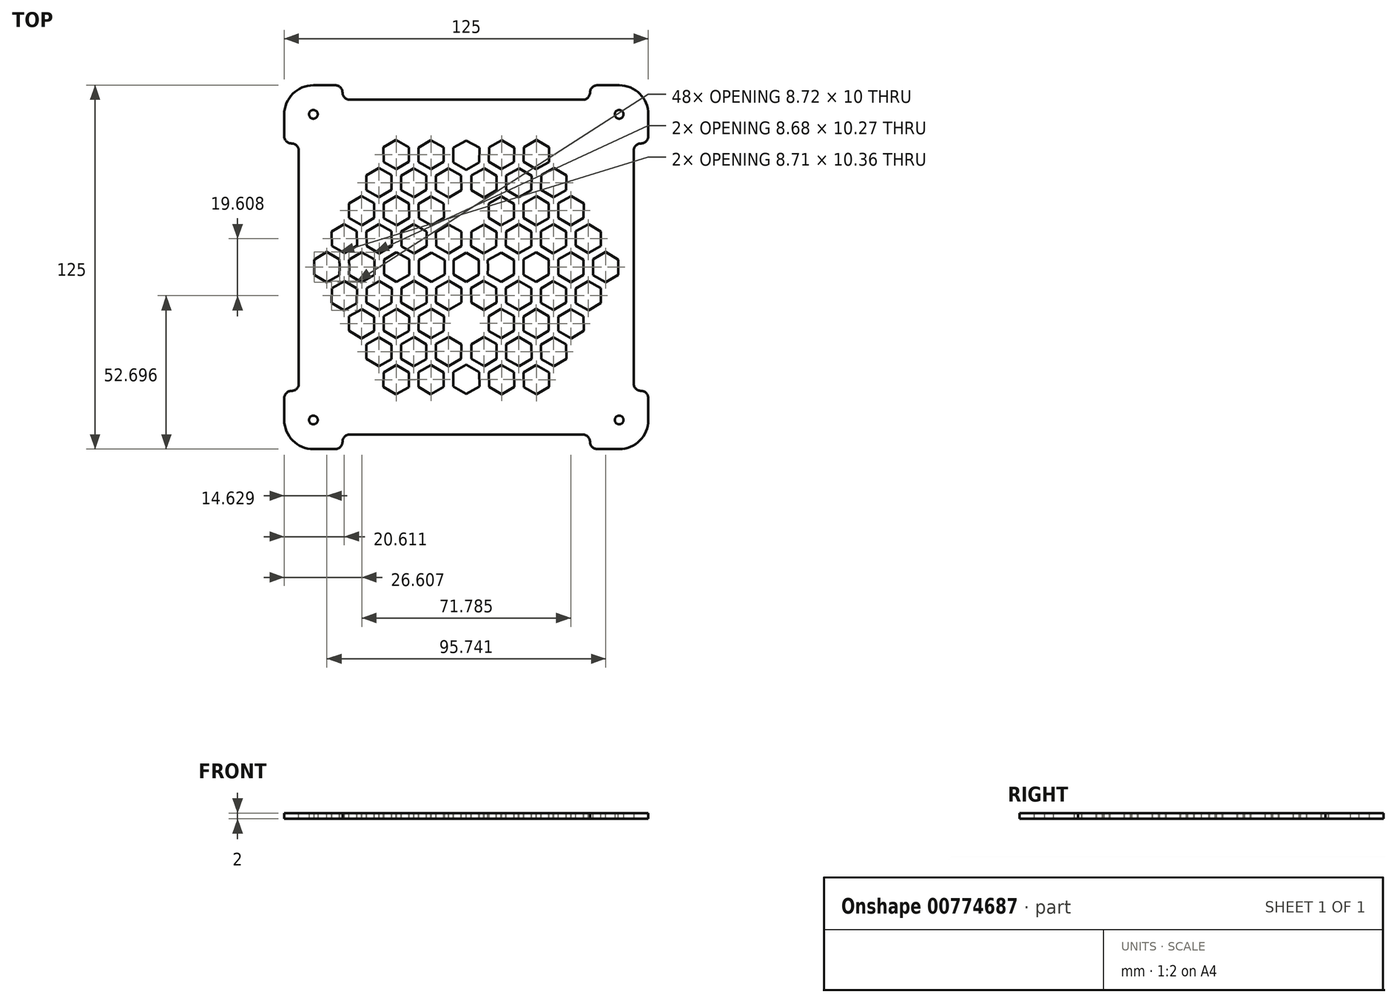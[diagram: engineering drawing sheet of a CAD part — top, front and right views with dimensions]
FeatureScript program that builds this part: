
annotation { "Feature Type Name" : "Feature", "Feature Type Description" : "" }
export const myFeature = defineFeature(function(context is Context, id is Id, definition is map)
    precondition{}
    {
        {
            var Q0;
            Q0=qCreatedBy(makeId("Top.planeOp"),FACE);
            var sketch = newSketch(context, id + "F0", { "sketchPlane" : qUnion([Q0])});
            skLineSegment(sketch, "E0.bottom", {"start": v(-52.5, 52.5) * mm, "end": v(52.5, 52.5) * mm});
            skLineSegment(sketch, "E0.top", {"start": v(-52.5, -52.5) * mm, "end": v(52.5, -52.5) * mm});
            skLineSegment(sketch, "E0.left", {"start": v(-52.5, 52.5) * mm, "end": v(-52.5, -52.5) * mm});
            skLineSegment(sketch, "E0.right", {"start": v(52.5, 52.5) * mm, "end": v(52.5, -52.5) * mm});
            skPoint(sketch, "E0.middle", {"position": v(0, 0) * mm});
            skCircle(sketch, "E1", {"center": v(0, 0) * mm, "radius": 52.5 * mm});
            skCircle(sketch, "E2", {"center": v(-52.5, 52.5) * mm, "radius": 1.5 * mm});
            skCircle(sketch, "E3", {"center": v(52.5, 52.5) * mm, "radius": 1.5 * mm});
            skCircle(sketch, "E4", {"center": v(52.5, -52.5) * mm, "radius": 1.5 * mm});
            skCircle(sketch, "E5", {"center": v(-52.5, -52.5) * mm, "radius": 1.5 * mm});
            skLineSegment(sketch, "E6.bottom", {"start": v(-62.5, 62.5) * mm, "end": v(-42.5, 62.5) * mm});
            skLineSegment(sketch, "E6.top", {"start": v(-62.5, 42.5) * mm, "end": v(-42.5, 42.5) * mm});
            skLineSegment(sketch, "E6.left", {"start": v(-62.5, 62.5) * mm, "end": v(-62.5, 42.5) * mm});
            skLineSegment(sketch, "E6.right", {"start": v(-42.5, 62.5) * mm, "end": v(-42.5, 42.5) * mm});
            skLineSegment(sketch, "E7.bottom", {"start": v(62.5, 62.5) * mm, "end": v(42.5, 62.5) * mm});
            skLineSegment(sketch, "E7.top", {"start": v(62.5, 42.5) * mm, "end": v(42.5, 42.5) * mm});
            skLineSegment(sketch, "E7.left", {"start": v(62.5, 62.5) * mm, "end": v(62.5, 42.5) * mm});
            skLineSegment(sketch, "E7.right", {"start": v(42.5, 62.5) * mm, "end": v(42.5, 42.5) * mm});
            skLineSegment(sketch, "E8.bottom", {"start": v(62.5, -42.5) * mm, "end": v(42.5, -42.5) * mm});
            skLineSegment(sketch, "E8.top", {"start": v(62.5, -62.5) * mm, "end": v(42.5, -62.5) * mm});
            skLineSegment(sketch, "E8.left", {"start": v(62.5, -42.5) * mm, "end": v(62.5, -62.5) * mm});
            skLineSegment(sketch, "E8.right", {"start": v(42.5, -42.5) * mm, "end": v(42.5, -62.5) * mm});
            skLineSegment(sketch, "E9.bottom", {"start": v(-62.5, -42.5) * mm, "end": v(-42.5, -42.5) * mm});
            skLineSegment(sketch, "E9.top", {"start": v(-62.5, -62.5) * mm, "end": v(-42.5, -62.5) * mm});
            skLineSegment(sketch, "E9.left", {"start": v(-62.5, -42.5) * mm, "end": v(-62.5, -62.5) * mm});
            skLineSegment(sketch, "E9.right", {"start": v(-42.5, -42.5) * mm, "end": v(-42.5, -62.5) * mm});
            skFitSpline(sketch, "E10", {"points": [v(0, 75.36) * mm, v(0, -75.45) * mm], "startDerivative": vector(0, -150.8) * mm, "endDerivative": vector(0, -150.8) * mm, "construction": true});
            skFitSpline(sketch, "E11", {"points": [v(-75.08, 0) * mm, v(75.41, 0) * mm], "startDerivative": vector(150.49, 0) * mm, "endDerivative": vector(150.49, 0) * mm, "construction": true});
            skLineSegment(sketch, "E12.bottom", {"start": v(-57.5, 57.5) * mm, "end": v(57.5, 57.5) * mm});
            skLineSegment(sketch, "E12.top", {"start": v(-57.5, -57.5) * mm, "end": v(57.5, -57.5) * mm});
            skLineSegment(sketch, "E12.left", {"start": v(-57.5, 57.5) * mm, "end": v(-57.5, -57.5) * mm});
            skLineSegment(sketch, "E12.right", {"start": v(57.5, 57.5) * mm, "end": v(57.5, -57.5) * mm});
            skSolve(sketch);
        }
        {
            var Q0;
            {var subQ0=sQuery(id+"F0.wireOp",EDGE,"E1");var subQ1=makeQuery(id+"F0.imprint","INTERSECT",VERTEX,{"derivedFrom":[sQuery(id+"F0.wireOp",EDGE,"E0.bottom"),subQ0]});Q0=makeQuery(id+"F0.imprint","IMPRINT",FACE,{"disambiguationData":[TD([[makeQuery(id+"F0.imprint","IMPRINT",EDGE,{"disambiguationData":[TD([[subQ1,1.0]])],"derivedFrom":subQ0}),1.0]])]});}
            var sketch = newSketch(context, id + "F1", { "sketchPlane" : qUnion([Q0])});
            skLineSegment(sketch, "E13.0", {"start": v(-4.36, 2.45) * mm, "end": v(0, 5) * mm});
            skLineSegment(sketch, "E13.5", {"start": v(-4.36, 0) * mm, "end": v(-4.36, 2.45) * mm});
            skPoint(sketch, "E13.0.midPoint", {"position": v(-2.18, 3.73) * mm});
            skLineSegment(sketch, "E14.1.0.0", {"start": v(-16.32, 2.5) * mm, "end": v(-12.02, 5.05) * mm});
            skLineSegment(sketch, "E14.1.0.2", {"start": v(-16.33, 0) * mm, "end": v(-16.32, 2.5) * mm});
            skLineSegment(sketch, "E14.1.0.4", {"start": v(-7.4, 2.45) * mm, "end": v(-7.42, 0) * mm});
            skLineSegment(sketch, "E14.1.0.5", {"start": v(-12.02, 5.05) * mm, "end": v(-7.4, 2.45) * mm});
            skLineSegment(sketch, "E14.1.1.0", {"start": v(-10.37, 12.12) * mm, "end": v(-6.07, 14.67) * mm});
            skLineSegment(sketch, "E14.1.1.1", {"start": v(-5.96, 4.67) * mm, "end": v(-10.32, 7.12) * mm});
            skLineSegment(sketch, "E14.1.1.2", {"start": v(-10.32, 7.12) * mm, "end": v(-10.37, 12.12) * mm});
            skLineSegment(sketch, "E14.1.1.3", {"start": v(-1.66, 7.22) * mm, "end": v(-5.96, 4.67) * mm});
            skLineSegment(sketch, "E14.1.1.4", {"start": v(-1.71, 12.22) * mm, "end": v(-1.66, 7.22) * mm});
            skLineSegment(sketch, "E14.1.1.5", {"start": v(-6.07, 14.67) * mm, "end": v(-1.71, 12.22) * mm});
            skLineSegment(sketch, "E14.1.2.0", {"start": v(-4.43, 21.74) * mm, "end": v(0, 24.24) * mm});
            skLineSegment(sketch, "E14.1.2.1", {"start": v(-0.02, 14.29) * mm, "end": v(-4.37, 16.74) * mm});
            skLineSegment(sketch, "E14.1.2.2", {"start": v(-4.37, 16.74) * mm, "end": v(-4.43, 21.74) * mm});
            skLineSegment(sketch, "E14.2.0.0", {"start": v(-28.27, 2.54) * mm, "end": v(-23.97, 5.1) * mm});
            skLineSegment(sketch, "E14.2.0.2", {"start": v(-28.28, 0) * mm, "end": v(-28.27, 2.54) * mm});
            skLineSegment(sketch, "E14.2.0.4", {"start": v(-19.61, 2.64) * mm, "end": v(-19.63, 0) * mm});
            skLineSegment(sketch, "E14.2.0.5", {"start": v(-23.97, 5.1) * mm, "end": v(-19.61, 2.64) * mm});
            skLineSegment(sketch, "E14.2.1.0", {"start": v(-22.33, 12.16) * mm, "end": v(-18.03, 14.71) * mm});
            skLineSegment(sketch, "E14.2.1.1", {"start": v(-17.92, 4.71) * mm, "end": v(-22.27, 7.16) * mm});
            skLineSegment(sketch, "E14.2.1.2", {"start": v(-22.27, 7.16) * mm, "end": v(-22.33, 12.16) * mm});
            skLineSegment(sketch, "E14.2.1.3", {"start": v(-13.61, 7.26) * mm, "end": v(-17.92, 4.71) * mm});
            skLineSegment(sketch, "E14.2.1.4", {"start": v(-13.67, 12.26) * mm, "end": v(-13.61, 7.26) * mm});
            skLineSegment(sketch, "E14.2.1.5", {"start": v(-18.03, 14.71) * mm, "end": v(-13.67, 12.26) * mm});
            skLineSegment(sketch, "E14.2.2.0", {"start": v(-16.39, 21.79) * mm, "end": v(-12.09, 24.33) * mm});
            skLineSegment(sketch, "E14.2.2.1", {"start": v(-11.97, 14.33) * mm, "end": v(-16.33, 16.79) * mm});
            skLineSegment(sketch, "E14.2.2.2", {"start": v(-16.33, 16.79) * mm, "end": v(-16.39, 21.79) * mm});
            skLineSegment(sketch, "E14.2.2.3", {"start": v(-7.67, 16.88) * mm, "end": v(-11.97, 14.33) * mm});
            skLineSegment(sketch, "E14.2.2.4", {"start": v(-7.73, 21.88) * mm, "end": v(-7.67, 16.88) * mm});
            skLineSegment(sketch, "E14.2.2.5", {"start": v(-12.09, 24.33) * mm, "end": v(-7.73, 21.88) * mm});
            skLineSegment(sketch, "E14.2.3.0", {"start": v(-10.45, 31.4) * mm, "end": v(-6.14, 33.96) * mm});
            skLineSegment(sketch, "E14.2.3.1", {"start": v(-6.03, 23.96) * mm, "end": v(-10.39, 26.4) * mm});
            skLineSegment(sketch, "E14.2.3.2", {"start": v(-10.39, 26.4) * mm, "end": v(-10.45, 31.4) * mm});
            skLineSegment(sketch, "E14.2.3.3", {"start": v(-1.73, 26.5) * mm, "end": v(-6.03, 23.96) * mm});
            skLineSegment(sketch, "E14.2.3.4", {"start": v(-1.79, 31.5) * mm, "end": v(-1.73, 26.5) * mm});
            skLineSegment(sketch, "E14.2.3.5", {"start": v(-6.14, 33.96) * mm, "end": v(-1.79, 31.5) * mm});
            skLineSegment(sketch, "E14.2.4.0", {"start": v(-4.5, 41.03) * mm, "end": v(0, 43.53) * mm});
            skLineSegment(sketch, "E14.2.4.1", {"start": v(0, 33.48) * mm, "end": v(-4.45, 36.03) * mm});
            skLineSegment(sketch, "E14.2.4.2", {"start": v(-4.45, 36.03) * mm, "end": v(-4.5, 41.03) * mm});
            skLineSegment(sketch, "E14.3.0.0", {"start": v(-40.23, 2.59) * mm, "end": v(-35.93, 5.14) * mm});
            skLineSegment(sketch, "E14.3.0.2", {"start": v(-40.22, 0) * mm, "end": v(-40.23, 2.59) * mm});
            skLineSegment(sketch, "E14.3.0.4", {"start": v(-31.57, 2.69) * mm, "end": v(-31.55, 0) * mm});
            skLineSegment(sketch, "E14.3.0.5", {"start": v(-35.93, 5.14) * mm, "end": v(-31.57, 2.69) * mm});
            skLineSegment(sketch, "E14.3.1.0", {"start": v(-34.29, 12.2) * mm, "end": v(-29.99, 14.76) * mm});
            skLineSegment(sketch, "E14.3.1.1", {"start": v(-29.87, 4.76) * mm, "end": v(-34.23, 7.2) * mm});
            skLineSegment(sketch, "E14.3.1.2", {"start": v(-34.23, 7.2) * mm, "end": v(-34.29, 12.2) * mm});
            skLineSegment(sketch, "E14.3.1.3", {"start": v(-25.57, 7.3) * mm, "end": v(-29.87, 4.76) * mm});
            skLineSegment(sketch, "E14.3.1.4", {"start": v(-25.63, 12.3) * mm, "end": v(-25.57, 7.3) * mm});
            skLineSegment(sketch, "E14.3.1.5", {"start": v(-29.99, 14.76) * mm, "end": v(-25.63, 12.3) * mm});
            skLineSegment(sketch, "E14.3.2.0", {"start": v(-28.35, 21.83) * mm, "end": v(-24.05, 24.38) * mm});
            skLineSegment(sketch, "E14.3.2.1", {"start": v(-23.93, 14.38) * mm, "end": v(-28.29, 16.83) * mm});
            skLineSegment(sketch, "E14.3.2.2", {"start": v(-28.29, 16.83) * mm, "end": v(-28.35, 21.83) * mm});
            skLineSegment(sketch, "E14.3.2.3", {"start": v(-19.63, 16.93) * mm, "end": v(-23.93, 14.38) * mm});
            skLineSegment(sketch, "E14.3.2.4", {"start": v(-19.69, 21.93) * mm, "end": v(-19.63, 16.93) * mm});
            skLineSegment(sketch, "E14.3.2.5", {"start": v(-24.05, 24.38) * mm, "end": v(-19.69, 21.93) * mm});
            skLineSegment(sketch, "E14.3.3.0", {"start": v(-22.4, 31.45) * mm, "end": v(-18.1, 34) * mm});
            skLineSegment(sketch, "E14.3.3.1", {"start": v(-17.99, 24) * mm, "end": v(-22.35, 26.45) * mm});
            skLineSegment(sketch, "E14.3.3.2", {"start": v(-22.35, 26.45) * mm, "end": v(-22.4, 31.45) * mm});
            skLineSegment(sketch, "E14.3.3.3", {"start": v(-13.69, 26.55) * mm, "end": v(-17.99, 24) * mm});
            skLineSegment(sketch, "E14.3.3.4", {"start": v(-13.74, 31.55) * mm, "end": v(-13.69, 26.55) * mm});
            skLineSegment(sketch, "E14.3.3.5", {"start": v(-18.1, 34) * mm, "end": v(-13.74, 31.55) * mm});
            skLineSegment(sketch, "E14.3.4.0", {"start": v(-16.46, 41.07) * mm, "end": v(-12.16, 43.62) * mm});
            skLineSegment(sketch, "E14.3.4.1", {"start": v(-12.05, 33.62) * mm, "end": v(-16.4, 36.07) * mm});
            skLineSegment(sketch, "E14.3.4.2", {"start": v(-16.4, 36.07) * mm, "end": v(-16.46, 41.07) * mm});
            skLineSegment(sketch, "E14.3.4.3", {"start": v(-7.74, 36.17) * mm, "end": v(-12.05, 33.62) * mm});
            skLineSegment(sketch, "E14.3.4.4", {"start": v(-7.8, 41.17) * mm, "end": v(-7.74, 36.17) * mm});
            skLineSegment(sketch, "E14.3.4.5", {"start": v(-12.16, 43.62) * mm, "end": v(-7.8, 41.17) * mm});
            skLineSegment(sketch, "E14.4.0.0", {"start": v(-52.19, 2.63) * mm, "end": v(-47.89, 5.18) * mm});
            skLineSegment(sketch, "E14.4.0.2", {"start": v(-52.23, 0) * mm, "end": v(-52.19, 2.63) * mm});
            skLineSegment(sketch, "E14.4.0.4", {"start": v(-43.53, 2.73) * mm, "end": v(-43.51, 0) * mm});
            skLineSegment(sketch, "E14.4.0.5", {"start": v(-47.89, 5.18) * mm, "end": v(-43.53, 2.73) * mm});
            skLineSegment(sketch, "E14.4.1.0", {"start": v(-46.25, 12.25) * mm, "end": v(-41.95, 14.8) * mm});
            skLineSegment(sketch, "E14.4.1.1", {"start": v(-41.83, 4.8) * mm, "end": v(-46.2, 7.25) * mm});
            skLineSegment(sketch, "E14.4.1.2", {"start": v(-46.2, 7.25) * mm, "end": v(-46.25, 12.25) * mm});
            skLineSegment(sketch, "E14.4.1.3", {"start": v(-37.53, 7.35) * mm, "end": v(-41.83, 4.8) * mm});
            skLineSegment(sketch, "E14.4.1.4", {"start": v(-37.59, 12.35) * mm, "end": v(-37.53, 7.35) * mm});
            skLineSegment(sketch, "E14.4.1.5", {"start": v(-41.95, 14.8) * mm, "end": v(-37.59, 12.35) * mm});
            skLineSegment(sketch, "E14.4.2.0", {"start": v(-40.3, 21.88) * mm, "end": v(-36, 24.43) * mm});
            skLineSegment(sketch, "E14.4.2.1", {"start": v(-35.89, 14.43) * mm, "end": v(-40.25, 16.88) * mm});
            skLineSegment(sketch, "E14.4.2.2", {"start": v(-40.25, 16.88) * mm, "end": v(-40.3, 21.88) * mm});
            skLineSegment(sketch, "E14.4.2.3", {"start": v(-31.59, 16.98) * mm, "end": v(-35.89, 14.43) * mm});
            skLineSegment(sketch, "E14.4.2.4", {"start": v(-31.64, 21.97) * mm, "end": v(-31.59, 16.98) * mm});
            skLineSegment(sketch, "E14.4.2.5", {"start": v(-36, 24.43) * mm, "end": v(-31.64, 21.97) * mm});
            skLineSegment(sketch, "E14.4.3.0", {"start": v(-34.36, 31.5) * mm, "end": v(-30.06, 34.05) * mm});
            skLineSegment(sketch, "E14.4.3.1", {"start": v(-29.95, 24.05) * mm, "end": v(-34.3, 26.5) * mm});
            skLineSegment(sketch, "E14.4.3.2", {"start": v(-34.3, 26.5) * mm, "end": v(-34.36, 31.5) * mm});
            skLineSegment(sketch, "E14.4.3.3", {"start": v(-25.65, 26.6) * mm, "end": v(-29.95, 24.05) * mm});
            skLineSegment(sketch, "E14.4.3.4", {"start": v(-25.7, 31.6) * mm, "end": v(-25.65, 26.6) * mm});
            skLineSegment(sketch, "E14.4.3.5", {"start": v(-30.06, 34.05) * mm, "end": v(-25.7, 31.6) * mm});
            skLineSegment(sketch, "E14.4.4.0", {"start": v(-28.42, 41.12) * mm, "end": v(-24.12, 43.67) * mm});
            skLineSegment(sketch, "E14.4.4.1", {"start": v(-24, 33.67) * mm, "end": v(-28.36, 36.12) * mm});
            skLineSegment(sketch, "E14.4.4.2", {"start": v(-28.36, 36.12) * mm, "end": v(-28.42, 41.12) * mm});
            skLineSegment(sketch, "E14.4.4.3", {"start": v(-19.7, 36.22) * mm, "end": v(-24, 33.67) * mm});
            skLineSegment(sketch, "E14.4.4.4", {"start": v(-19.76, 41.22) * mm, "end": v(-19.7, 36.22) * mm});
            skLineSegment(sketch, "E14.4.4.5", {"start": v(-24.12, 43.67) * mm, "end": v(-19.76, 41.22) * mm});
            skLineSegment(sketch, "E15.MirrorCS", {"start": v(4.36, 0) * mm, "end": v(4.36, 2.45) * mm});
            skLineSegment(sketch, "E16.MirrorCS", {"start": v(40.25, 16.88) * mm, "end": v(40.3, 21.88) * mm});
            skLineSegment(sketch, "E17.MirrorCS", {"start": v(4.45, 36.03) * mm, "end": v(4.5, 41.03) * mm});
            skLineSegment(sketch, "E18.MirrorCS", {"start": v(24, 33.67) * mm, "end": v(28.36, 36.12) * mm});
            skLineSegment(sketch, "E19.MirrorCS", {"start": v(12.16, 43.62) * mm, "end": v(7.8, 41.17) * mm});
            skLineSegment(sketch, "E20.MirrorCS", {"start": v(1.79, 31.5) * mm, "end": v(1.73, 26.5) * mm});
            skLineSegment(sketch, "E21.MirrorCS", {"start": v(28.35, 21.83) * mm, "end": v(24.05, 24.38) * mm});
            skLineSegment(sketch, "E22.MirrorCS", {"start": v(23.93, 14.38) * mm, "end": v(28.29, 16.83) * mm});
            skLineSegment(sketch, "E23.MirrorCS", {"start": v(41.83, 4.8) * mm, "end": v(46.2, 7.25) * mm});
            skLineSegment(sketch, "E24.MirrorCS", {"start": v(17.92, 4.71) * mm, "end": v(22.27, 7.16) * mm});
            skLineSegment(sketch, "E25.MirrorCS", {"start": v(17.99, 24) * mm, "end": v(22.35, 26.45) * mm});
            skLineSegment(sketch, "E26.MirrorCS", {"start": v(35.89, 14.43) * mm, "end": v(40.25, 16.88) * mm});
            skLineSegment(sketch, "E27.MirrorCS", {"start": v(40.22, 0) * mm, "end": v(40.23, 2.59) * mm});
            skLineSegment(sketch, "E28.MirrorCS", {"start": v(30.06, 34.05) * mm, "end": v(25.7, 31.6) * mm});
            skLineSegment(sketch, "E29.MirrorCS", {"start": v(16.46, 41.07) * mm, "end": v(12.16, 43.62) * mm});
            skLineSegment(sketch, "E30.MirrorCS", {"start": v(16.39, 21.79) * mm, "end": v(12.09, 24.33) * mm});
            skLineSegment(sketch, "E31.MirrorCS", {"start": v(34.3, 26.5) * mm, "end": v(34.36, 31.5) * mm});
            skLineSegment(sketch, "E32.MirrorCS", {"start": v(37.59, 12.35) * mm, "end": v(37.53, 7.35) * mm});
            skLineSegment(sketch, "E33.MirrorCS", {"start": v(28.36, 36.12) * mm, "end": v(28.42, 41.12) * mm});
            skLineSegment(sketch, "E34.MirrorCS", {"start": v(7.67, 16.88) * mm, "end": v(11.97, 14.33) * mm});
            skLineSegment(sketch, "E35.MirrorCS", {"start": v(10.45, 31.4) * mm, "end": v(6.14, 33.96) * mm});
            skLineSegment(sketch, "E36.MirrorCS", {"start": v(41.95, 14.8) * mm, "end": v(37.59, 12.35) * mm});
            skLineSegment(sketch, "E37.MirrorCS", {"start": v(31.57, 2.69) * mm, "end": v(31.55, 0) * mm});
            skLineSegment(sketch, "E38.MirrorCS", {"start": v(22.35, 26.45) * mm, "end": v(22.4, 31.45) * mm});
            skLineSegment(sketch, "E39.MirrorCS", {"start": v(46.2, 7.25) * mm, "end": v(46.25, 12.25) * mm});
            skLineSegment(sketch, "E40.MirrorCS", {"start": v(28.42, 41.12) * mm, "end": v(24.12, 43.67) * mm});
            skLineSegment(sketch, "E41.MirrorCS", {"start": v(11.97, 14.33) * mm, "end": v(16.33, 16.79) * mm});
            skLineSegment(sketch, "E42.MirrorCS", {"start": v(19.7, 36.22) * mm, "end": v(24, 33.67) * mm});
            skLineSegment(sketch, "E43.MirrorCS", {"start": v(19.76, 41.22) * mm, "end": v(19.7, 36.22) * mm});
            skLineSegment(sketch, "E44.MirrorCS", {"start": v(7.8, 41.17) * mm, "end": v(7.74, 36.17) * mm});
            skLineSegment(sketch, "E45.MirrorCS", {"start": v(31.64, 21.97) * mm, "end": v(31.59, 16.98) * mm});
            skLineSegment(sketch, "E46.MirrorCS", {"start": v(7.74, 36.17) * mm, "end": v(12.05, 33.62) * mm});
            skLineSegment(sketch, "E47.MirrorCS", {"start": v(19.61, 2.64) * mm, "end": v(19.63, 0) * mm});
            skLineSegment(sketch, "E48.MirrorCS", {"start": v(18.1, 34) * mm, "end": v(13.74, 31.55) * mm});
            skLineSegment(sketch, "E49.MirrorCS", {"start": v(25.57, 7.3) * mm, "end": v(29.87, 4.76) * mm});
            skLineSegment(sketch, "E50.MirrorCS", {"start": v(19.69, 21.93) * mm, "end": v(19.63, 16.93) * mm});
            skLineSegment(sketch, "E51.MirrorCS", {"start": v(24.12, 43.67) * mm, "end": v(19.76, 41.22) * mm});
            skLineSegment(sketch, "E52.MirrorCS", {"start": v(16.33, 16.79) * mm, "end": v(16.39, 21.79) * mm});
            skLineSegment(sketch, "E53.MirrorCS", {"start": v(22.27, 7.16) * mm, "end": v(22.33, 12.16) * mm});
            skLineSegment(sketch, "E54.MirrorCS", {"start": v(13.74, 31.55) * mm, "end": v(13.69, 26.55) * mm});
            skLineSegment(sketch, "E55.MirrorCS", {"start": v(34.23, 7.2) * mm, "end": v(34.29, 12.2) * mm});
            skLineSegment(sketch, "E56.MirrorCS", {"start": v(34.36, 31.5) * mm, "end": v(30.06, 34.05) * mm});
            skLineSegment(sketch, "E57.MirrorCS", {"start": v(13.61, 7.26) * mm, "end": v(17.92, 4.71) * mm});
            skLineSegment(sketch, "E58.MirrorCS", {"start": v(36, 24.43) * mm, "end": v(31.64, 21.97) * mm});
            skLineSegment(sketch, "E59.MirrorCS", {"start": v(22.33, 12.16) * mm, "end": v(18.03, 14.71) * mm});
            skLineSegment(sketch, "E60.MirrorCS", {"start": v(43.53, 2.73) * mm, "end": v(43.51, 0) * mm});
            skLineSegment(sketch, "E61.MirrorCS", {"start": v(12.05, 33.62) * mm, "end": v(16.4, 36.07) * mm});
            skLineSegment(sketch, "E62.MirrorCS", {"start": v(52.19, 2.63) * mm, "end": v(47.89, 5.18) * mm});
            skLineSegment(sketch, "E63.MirrorCS", {"start": v(52.23, 0) * mm, "end": v(52.19, 2.63) * mm});
            skLineSegment(sketch, "E64.MirrorCS", {"start": v(29.95, 24.05) * mm, "end": v(34.3, 26.5) * mm});
            skLineSegment(sketch, "E65.MirrorCS", {"start": v(40.3, 21.88) * mm, "end": v(36, 24.43) * mm});
            skLineSegment(sketch, "E66.MirrorCS", {"start": v(10.37, 12.12) * mm, "end": v(6.07, 14.67) * mm});
            skLineSegment(sketch, "E67.MirrorCS", {"start": v(22.4, 31.45) * mm, "end": v(18.1, 34) * mm});
            skLineSegment(sketch, "E68.MirrorCS", {"start": v(1.66, 7.22) * mm, "end": v(5.96, 4.67) * mm});
            skLineSegment(sketch, "E69.MirrorCS", {"start": v(35.93, 5.14) * mm, "end": v(31.57, 2.69) * mm});
            skLineSegment(sketch, "E70.MirrorCS", {"start": v(1.71, 12.22) * mm, "end": v(1.66, 7.22) * mm});
            skLineSegment(sketch, "E71.MirrorCS", {"start": v(7.4, 2.45) * mm, "end": v(7.42, 0) * mm});
            skLineSegment(sketch, "E72.MirrorCS", {"start": v(12.02, 5.05) * mm, "end": v(7.4, 2.45) * mm});
            skLineSegment(sketch, "E73.MirrorCS", {"start": v(25.7, 31.6) * mm, "end": v(25.65, 26.6) * mm});
            skLineSegment(sketch, "E74.MirrorCS", {"start": v(29.99, 14.76) * mm, "end": v(25.63, 12.3) * mm});
            skLineSegment(sketch, "E75.MirrorCS", {"start": v(10.32, 7.12) * mm, "end": v(10.37, 12.12) * mm});
            skLineSegment(sketch, "E76.MirrorCS", {"start": v(6.14, 33.96) * mm, "end": v(1.79, 31.5) * mm});
            skLineSegment(sketch, "E77.MirrorCS", {"start": v(25.63, 12.3) * mm, "end": v(25.57, 7.3) * mm});
            skLineSegment(sketch, "E78.MirrorCS", {"start": v(4.37, 16.74) * mm, "end": v(4.43, 21.74) * mm});
            skLineSegment(sketch, "E79.MirrorCS", {"start": v(28.27, 2.54) * mm, "end": v(23.97, 5.1) * mm});
            skLineSegment(sketch, "E80.MirrorCS", {"start": v(6.03, 23.96) * mm, "end": v(10.39, 26.4) * mm});
            skLineSegment(sketch, "E81.MirrorCS", {"start": v(29.87, 4.76) * mm, "end": v(34.23, 7.2) * mm});
            skLineSegment(sketch, "E82.MirrorCS", {"start": v(25.65, 26.6) * mm, "end": v(29.95, 24.05) * mm});
            skLineSegment(sketch, "E83.MirrorCS", {"start": v(13.69, 26.55) * mm, "end": v(17.99, 24) * mm});
            skLineSegment(sketch, "E84.MirrorCS", {"start": v(34.29, 12.2) * mm, "end": v(29.99, 14.76) * mm});
            skLineSegment(sketch, "E85.MirrorCS", {"start": v(37.53, 7.35) * mm, "end": v(41.83, 4.8) * mm});
            skLineSegment(sketch, "E86.MirrorCS", {"start": v(19.63, 16.93) * mm, "end": v(23.93, 14.38) * mm});
            skLineSegment(sketch, "E87.MirrorCS", {"start": v(12.09, 24.33) * mm, "end": v(7.73, 21.88) * mm});
            skLineSegment(sketch, "E88.MirrorCS", {"start": v(16.4, 36.07) * mm, "end": v(16.46, 41.07) * mm});
            skLineSegment(sketch, "E89.MirrorCS", {"start": v(28.28, 0) * mm, "end": v(28.27, 2.54) * mm});
            skLineSegment(sketch, "E90.MirrorCS", {"start": v(47.89, 5.18) * mm, "end": v(43.53, 2.73) * mm});
            skLineSegment(sketch, "E91.MirrorCS", {"start": v(46.25, 12.25) * mm, "end": v(41.95, 14.8) * mm});
            skLineSegment(sketch, "E92.MirrorCS", {"start": v(7.73, 21.88) * mm, "end": v(7.67, 16.88) * mm});
            skLineSegment(sketch, "E93.MirrorCS", {"start": v(1.73, 26.5) * mm, "end": v(6.03, 23.96) * mm});
            skLineSegment(sketch, "E94.MirrorCS", {"start": v(16.33, 0) * mm, "end": v(16.32, 2.5) * mm});
            skLineSegment(sketch, "E95.MirrorCS", {"start": v(10.39, 26.4) * mm, "end": v(10.45, 31.4) * mm});
            skLineSegment(sketch, "E96.MirrorCS", {"start": v(6.07, 14.67) * mm, "end": v(1.71, 12.22) * mm});
            skLineSegment(sketch, "E97.MirrorCS", {"start": v(23.97, 5.1) * mm, "end": v(19.61, 2.64) * mm});
            skLineSegment(sketch, "E98.MirrorCS", {"start": v(13.67, 12.26) * mm, "end": v(13.61, 7.26) * mm});
            skLineSegment(sketch, "E99.MirrorCS", {"start": v(28.29, 16.83) * mm, "end": v(28.35, 21.83) * mm});
            skLineSegment(sketch, "E100.MirrorCS", {"start": v(31.59, 16.98) * mm, "end": v(35.89, 14.43) * mm});
            skLineSegment(sketch, "E101.MirrorCS", {"start": v(18.03, 14.71) * mm, "end": v(13.67, 12.26) * mm});
            skLineSegment(sketch, "E102.MirrorCS", {"start": v(40.23, 2.59) * mm, "end": v(35.93, 5.14) * mm});
            skLineSegment(sketch, "E103.MirrorCS", {"start": v(5.96, 4.67) * mm, "end": v(10.32, 7.12) * mm});
            skLineSegment(sketch, "E104.MirrorCS", {"start": v(16.32, 2.5) * mm, "end": v(12.02, 5.05) * mm});
            skLineSegment(sketch, "E105.MirrorCS", {"start": v(24.05, 24.38) * mm, "end": v(19.69, 21.93) * mm});
            skLineSegment(sketch, "E106.MirrorCS", {"start": v(4.43, 21.74) * mm, "end": v(0, 24.24) * mm});
            skLineSegment(sketch, "E107.MirrorCS", {"start": v(0, 33.48) * mm, "end": v(4.45, 36.03) * mm});
            skLineSegment(sketch, "E108.MirrorCS", {"start": v(4.5, 41.03) * mm, "end": v(0, 43.53) * mm});
            skLineSegment(sketch, "E109.MirrorCS", {"start": v(0.02, 14.29) * mm, "end": v(4.37, 16.74) * mm});
            skLineSegment(sketch, "E110.MirrorCS", {"start": v(4.36, 2.45) * mm, "end": v(0, 5) * mm});
            skPoint(sketch, "E111.MirrorP", {"position": v(2.18, 3.73) * mm});
            skLineSegment(sketch, "E112.MirrorCS", {"start": v(22.33, -12.16) * mm, "end": v(18.03, -14.71) * mm});
            skLineSegment(sketch, "E113.MirrorCS", {"start": v(19.76, -41.22) * mm, "end": v(19.7, -36.22) * mm});
            skLineSegment(sketch, "E114.MirrorCS", {"start": v(7.4, -2.45) * mm, "end": v(7.42, 0) * mm});
            skLineSegment(sketch, "E115.MirrorCS", {"start": v(0, -33.48) * mm, "end": v(4.45, -36.03) * mm});
            skLineSegment(sketch, "E116.MirrorCS", {"start": v(46.25, -12.25) * mm, "end": v(41.95, -14.8) * mm});
            skLineSegment(sketch, "E117.MirrorCS", {"start": v(-46.25, -12.25) * mm, "end": v(-41.95, -14.8) * mm});
            skLineSegment(sketch, "E118.MirrorCS", {"start": v(-19.76, -41.22) * mm, "end": v(-19.7, -36.22) * mm});
            skLineSegment(sketch, "E119.MirrorCS", {"start": v(35.93, -5.14) * mm, "end": v(31.57, -2.69) * mm});
            skLineSegment(sketch, "E120.MirrorCS", {"start": v(-40.3, -21.88) * mm, "end": v(-36, -24.43) * mm});
            skLineSegment(sketch, "E121.MirrorCS", {"start": v(28.35, -21.83) * mm, "end": v(24.05, -24.38) * mm});
            skLineSegment(sketch, "E122.MirrorCS", {"start": v(34.36, -31.5) * mm, "end": v(30.06, -34.05) * mm});
            skLineSegment(sketch, "E123.MirrorCS", {"start": v(28.42, -41.12) * mm, "end": v(24.12, -43.67) * mm});
            skLineSegment(sketch, "E124.MirrorCS", {"start": v(-46.2, -7.25) * mm, "end": v(-46.25, -12.25) * mm});
            skLineSegment(sketch, "E125.MirrorCS", {"start": v(4.5, -41.03) * mm, "end": v(0, -43.53) * mm});
            skLineSegment(sketch, "E126.MirrorCS", {"start": v(30.06, -34.05) * mm, "end": v(25.7, -31.6) * mm});
            skLineSegment(sketch, "E127.MirrorCS", {"start": v(-28.42, -41.12) * mm, "end": v(-24.12, -43.67) * mm});
            skLineSegment(sketch, "E128.MirrorCS", {"start": v(-7.67, -16.88) * mm, "end": v(-11.97, -14.33) * mm});
            skLineSegment(sketch, "E129.MirrorCS", {"start": v(-28.36, -36.12) * mm, "end": v(-28.42, -41.12) * mm});
            skLineSegment(sketch, "E130.MirrorCS", {"start": v(-37.59, -12.35) * mm, "end": v(-37.53, -7.35) * mm});
            skLineSegment(sketch, "E131.MirrorCS", {"start": v(-13.74, -31.55) * mm, "end": v(-13.69, -26.55) * mm});
            skLineSegment(sketch, "E132.MirrorCS", {"start": v(-11.97, -14.33) * mm, "end": v(-16.33, -16.79) * mm});
            skLineSegment(sketch, "E133.MirrorCS", {"start": v(-22.35, -26.45) * mm, "end": v(-22.4, -31.45) * mm});
            skLineSegment(sketch, "E134.MirrorCS", {"start": v(10.32, -7.12) * mm, "end": v(10.37, -12.12) * mm});
            skLineSegment(sketch, "E135.MirrorCS", {"start": v(-34.29, -12.2) * mm, "end": v(-29.99, -14.76) * mm});
            skLineSegment(sketch, "E136.MirrorCS", {"start": v(-28.29, -16.83) * mm, "end": v(-28.35, -21.83) * mm});
            skLineSegment(sketch, "E137.MirrorCS", {"start": v(-29.99, -14.76) * mm, "end": v(-25.63, -12.3) * mm});
            skLineSegment(sketch, "E138.MirrorCS", {"start": v(-6.07, -14.67) * mm, "end": v(-1.71, -12.22) * mm});
            skLineSegment(sketch, "E139.MirrorCS", {"start": v(-17.92, -4.71) * mm, "end": v(-22.27, -7.16) * mm});
            skLineSegment(sketch, "E140.MirrorCS", {"start": v(46.2, -7.25) * mm, "end": v(46.25, -12.25) * mm});
            skLineSegment(sketch, "E141.MirrorCS", {"start": v(-4.45, -36.03) * mm, "end": v(-4.5, -41.03) * mm});
            skLineSegment(sketch, "E142.MirrorCS", {"start": v(-24.05, -24.38) * mm, "end": v(-19.69, -21.93) * mm});
            skLineSegment(sketch, "E143.MirrorCS", {"start": v(-35.93, -5.14) * mm, "end": v(-31.57, -2.69) * mm});
            skLineSegment(sketch, "E144.MirrorCS", {"start": v(41.83, -4.8) * mm, "end": v(46.2, -7.25) * mm});
            skLineSegment(sketch, "E145.MirrorCS", {"start": v(-13.67, -12.26) * mm, "end": v(-13.61, -7.26) * mm});
            skLineSegment(sketch, "E146.MirrorCS", {"start": v(-37.53, -7.35) * mm, "end": v(-41.83, -4.8) * mm});
            skLineSegment(sketch, "E147.MirrorCS", {"start": v(-13.69, -26.55) * mm, "end": v(-17.99, -24) * mm});
            skLineSegment(sketch, "E148.MirrorCS", {"start": v(-34.36, -31.5) * mm, "end": v(-30.06, -34.05) * mm});
            skLineSegment(sketch, "E149.MirrorCS", {"start": v(-16.33, -16.79) * mm, "end": v(-16.39, -21.79) * mm});
            skLineSegment(sketch, "E150.MirrorCS", {"start": v(-52.19, -2.63) * mm, "end": v(-47.89, -5.18) * mm});
            skLineSegment(sketch, "E151.MirrorCS", {"start": v(-24, -33.67) * mm, "end": v(-28.36, -36.12) * mm});
            skLineSegment(sketch, "E152.MirrorCS", {"start": v(-1.66, -7.22) * mm, "end": v(-5.96, -4.67) * mm});
            skLineSegment(sketch, "E153.MirrorCS", {"start": v(-41.95, -14.8) * mm, "end": v(-37.59, -12.35) * mm});
            skLineSegment(sketch, "E154.MirrorCS", {"start": v(7.8, -41.17) * mm, "end": v(7.74, -36.17) * mm});
            skLineSegment(sketch, "E155.MirrorCS", {"start": v(-7.4, -2.45) * mm, "end": v(-7.42, 0) * mm});
            skLineSegment(sketch, "E156.MirrorCS", {"start": v(-41.83, -4.8) * mm, "end": v(-46.2, -7.25) * mm});
            skLineSegment(sketch, "E157.MirrorCS", {"start": v(-16.33, 0) * mm, "end": v(-16.32, -2.5) * mm});
            skLineSegment(sketch, "E158.MirrorCS", {"start": v(-7.73, -21.88) * mm, "end": v(-7.67, -16.88) * mm});
            skLineSegment(sketch, "E159.MirrorCS", {"start": v(13.69, -26.55) * mm, "end": v(17.99, -24) * mm});
            skLineSegment(sketch, "E160.MirrorCS", {"start": v(-16.32, -2.5) * mm, "end": v(-12.02, -5.05) * mm});
            skLineSegment(sketch, "E161.MirrorCS", {"start": v(29.99, -14.76) * mm, "end": v(25.63, -12.3) * mm});
            skLineSegment(sketch, "E162.MirrorCS", {"start": v(-4.36, 0) * mm, "end": v(-4.36, -2.45) * mm});
            skLineSegment(sketch, "E163.MirrorCS", {"start": v(18.1, -34) * mm, "end": v(13.74, -31.55) * mm});
            skLineSegment(sketch, "E164.MirrorCS", {"start": v(29.95, -24.05) * mm, "end": v(34.3, -26.5) * mm});
            skLineSegment(sketch, "E165.MirrorCS", {"start": v(-25.65, -26.6) * mm, "end": v(-29.95, -24.05) * mm});
            skLineSegment(sketch, "E166.MirrorCS", {"start": v(6.07, -14.67) * mm, "end": v(1.71, -12.22) * mm});
            skLineSegment(sketch, "E167.MirrorCS", {"start": v(-28.27, -2.54) * mm, "end": v(-23.97, -5.1) * mm});
            skLineSegment(sketch, "E168.MirrorCS", {"start": v(-4.37, -16.74) * mm, "end": v(-4.43, -21.74) * mm});
            skLineSegment(sketch, "E169.MirrorCS", {"start": v(-0.02, -14.29) * mm, "end": v(-4.37, -16.74) * mm});
            skLineSegment(sketch, "E170.MirrorCS", {"start": v(-17.99, -24) * mm, "end": v(-22.35, -26.45) * mm});
            skLineSegment(sketch, "E171.MirrorCS", {"start": v(0.02, -14.29) * mm, "end": v(4.37, -16.74) * mm});
            skLineSegment(sketch, "E172.MirrorCS", {"start": v(31.64, -21.97) * mm, "end": v(31.59, -16.98) * mm});
            skLineSegment(sketch, "E173.MirrorCS", {"start": v(12.05, -33.62) * mm, "end": v(16.4, -36.07) * mm});
            skLineSegment(sketch, "E174.MirrorCS", {"start": v(25.63, -12.3) * mm, "end": v(25.57, -7.3) * mm});
            skLineSegment(sketch, "E175.MirrorCS", {"start": v(1.73, -26.5) * mm, "end": v(6.03, -23.96) * mm});
            skLineSegment(sketch, "E176.MirrorCS", {"start": v(-16.46, -41.07) * mm, "end": v(-12.16, -43.62) * mm});
            skLineSegment(sketch, "E177.MirrorCS", {"start": v(-1.73, -26.5) * mm, "end": v(-6.03, -23.96) * mm});
            skLineSegment(sketch, "E178.MirrorCS", {"start": v(-28.35, -21.83) * mm, "end": v(-24.05, -24.38) * mm});
            skLineSegment(sketch, "E179.MirrorCS", {"start": v(-47.89, -5.18) * mm, "end": v(-43.53, -2.73) * mm});
            skLineSegment(sketch, "E180.MirrorCS", {"start": v(-30.06, -34.05) * mm, "end": v(-25.7, -31.6) * mm});
            skLineSegment(sketch, "E181.MirrorCS", {"start": v(-23.97, -5.1) * mm, "end": v(-19.61, -2.64) * mm});
            skLineSegment(sketch, "E182.MirrorCS", {"start": v(28.36, -36.12) * mm, "end": v(28.42, -41.12) * mm});
            skLineSegment(sketch, "E183.MirrorCS", {"start": v(4.45, -36.03) * mm, "end": v(4.5, -41.03) * mm});
            skLineSegment(sketch, "E184.MirrorCS", {"start": v(-31.64, -21.97) * mm, "end": v(-31.59, -16.98) * mm});
            skLineSegment(sketch, "E185.MirrorCS", {"start": v(16.46, -41.07) * mm, "end": v(12.16, -43.62) * mm});
            skLineSegment(sketch, "E186.MirrorCS", {"start": v(-12.09, -24.33) * mm, "end": v(-7.73, -21.88) * mm});
            skLineSegment(sketch, "E187.MirrorCS", {"start": v(-7.8, -41.17) * mm, "end": v(-7.74, -36.17) * mm});
            skLineSegment(sketch, "E188.MirrorCS", {"start": v(23.97, -5.1) * mm, "end": v(19.61, -2.64) * mm});
            skLineSegment(sketch, "E189.MirrorCS", {"start": v(29.87, -4.76) * mm, "end": v(34.23, -7.2) * mm});
            skLineSegment(sketch, "E190.MirrorCS", {"start": v(-16.39, -21.79) * mm, "end": v(-12.09, -24.33) * mm});
            skLineSegment(sketch, "E191.MirrorCS", {"start": v(40.3, -21.88) * mm, "end": v(36, -24.43) * mm});
            skLineSegment(sketch, "E192.MirrorCS", {"start": v(-7.74, -36.17) * mm, "end": v(-12.05, -33.62) * mm});
            skLineSegment(sketch, "E193.MirrorCS", {"start": v(40.25, -16.88) * mm, "end": v(40.3, -21.88) * mm});
            skLineSegment(sketch, "E194.MirrorCS", {"start": v(-31.59, -16.98) * mm, "end": v(-35.89, -14.43) * mm});
            skLineSegment(sketch, "E195.MirrorCS", {"start": v(-4.43, -21.74) * mm, "end": v(0, -24.24) * mm});
            skLineSegment(sketch, "E196.MirrorCS", {"start": v(37.59, -12.35) * mm, "end": v(37.53, -7.35) * mm});
            skLineSegment(sketch, "E197.MirrorCS", {"start": v(-34.23, -7.2) * mm, "end": v(-34.29, -12.2) * mm});
            skLineSegment(sketch, "E198.MirrorCS", {"start": v(-22.4, -31.45) * mm, "end": v(-18.1, -34) * mm});
            skLineSegment(sketch, "E199.MirrorCS", {"start": v(25.57, -7.3) * mm, "end": v(29.87, -4.76) * mm});
            skLineSegment(sketch, "E200.MirrorCS", {"start": v(24.12, -43.67) * mm, "end": v(19.76, -41.22) * mm});
            skLineSegment(sketch, "E201.MirrorCS", {"start": v(13.61, -7.26) * mm, "end": v(17.92, -4.71) * mm});
            skLineSegment(sketch, "E202.MirrorCS", {"start": v(-10.39, -26.4) * mm, "end": v(-10.45, -31.4) * mm});
            skLineSegment(sketch, "E203.MirrorCS", {"start": v(11.97, -14.33) * mm, "end": v(16.33, -16.79) * mm});
            skLineSegment(sketch, "E204.MirrorCS", {"start": v(24.05, -24.38) * mm, "end": v(19.69, -21.93) * mm});
            skLineSegment(sketch, "E205.MirrorCS", {"start": v(-40.23, -2.59) * mm, "end": v(-35.93, -5.14) * mm});
            skLineSegment(sketch, "E206.MirrorCS", {"start": v(34.23, -7.2) * mm, "end": v(34.29, -12.2) * mm});
            skLineSegment(sketch, "E207.MirrorCS", {"start": v(-1.71, -12.22) * mm, "end": v(-1.66, -7.22) * mm});
            skLineSegment(sketch, "E208.MirrorCS", {"start": v(-10.32, -7.12) * mm, "end": v(-10.37, -12.12) * mm});
            skLineSegment(sketch, "E209.MirrorCS", {"start": v(35.89, -14.43) * mm, "end": v(40.25, -16.88) * mm});
            skLineSegment(sketch, "E210.MirrorCS", {"start": v(19.63, -16.93) * mm, "end": v(23.93, -14.38) * mm});
            skLineSegment(sketch, "E211.MirrorCS", {"start": v(-18.1, -34) * mm, "end": v(-13.74, -31.55) * mm});
            skLineSegment(sketch, "E212.MirrorCS", {"start": v(-25.7, -31.6) * mm, "end": v(-25.65, -26.6) * mm});
            skLineSegment(sketch, "E213.MirrorCS", {"start": v(-5.96, -4.67) * mm, "end": v(-10.32, -7.12) * mm});
            skLineSegment(sketch, "E214.MirrorCS", {"start": v(-10.37, -12.12) * mm, "end": v(-6.07, -14.67) * mm});
            skLineSegment(sketch, "E215.MirrorCS", {"start": v(17.92, -4.71) * mm, "end": v(22.27, -7.16) * mm});
            skLineSegment(sketch, "E216.MirrorCS", {"start": v(16.32, -2.5) * mm, "end": v(12.02, -5.05) * mm});
            skLineSegment(sketch, "E217.MirrorCS", {"start": v(16.4, -36.07) * mm, "end": v(16.46, -41.07) * mm});
            skLineSegment(sketch, "E218.MirrorCS", {"start": v(-12.02, -5.05) * mm, "end": v(-7.4, -2.45) * mm});
            skLineSegment(sketch, "E219.MirrorCS", {"start": v(-4.36, -2.45) * mm, "end": v(0, -5) * mm});
            skLineSegment(sketch, "E220.MirrorCS", {"start": v(6.03, -23.96) * mm, "end": v(10.39, -26.4) * mm});
            skLineSegment(sketch, "E221.MirrorCS", {"start": v(12.02, -5.05) * mm, "end": v(7.4, -2.45) * mm});
            skLineSegment(sketch, "E222.MirrorCS", {"start": v(10.37, -12.12) * mm, "end": v(6.07, -14.67) * mm});
            skLineSegment(sketch, "E223.MirrorCS", {"start": v(25.65, -26.6) * mm, "end": v(29.95, -24.05) * mm});
            skLineSegment(sketch, "E224.MirrorCS", {"start": v(13.67, -12.26) * mm, "end": v(13.61, -7.26) * mm});
            skLineSegment(sketch, "E225.MirrorCS", {"start": v(-12.16, -43.62) * mm, "end": v(-7.8, -41.17) * mm});
            skLineSegment(sketch, "E226.MirrorCS", {"start": v(-36, -24.43) * mm, "end": v(-31.64, -21.97) * mm});
            skLineSegment(sketch, "E227.MirrorCS", {"start": v(24, -33.67) * mm, "end": v(28.36, -36.12) * mm});
            skLineSegment(sketch, "E228.MirrorCS", {"start": v(36, -24.43) * mm, "end": v(31.64, -21.97) * mm});
            skLineSegment(sketch, "E229.MirrorCS", {"start": v(19.7, -36.22) * mm, "end": v(24, -33.67) * mm});
            skLineSegment(sketch, "E230.MirrorCS", {"start": v(7.67, -16.88) * mm, "end": v(11.97, -14.33) * mm});
            skLineSegment(sketch, "E231.MirrorCS", {"start": v(-22.33, -12.16) * mm, "end": v(-18.03, -14.71) * mm});
            skLineSegment(sketch, "E232.MirrorCS", {"start": v(1.71, -12.22) * mm, "end": v(1.66, -7.22) * mm});
            skLineSegment(sketch, "E233.MirrorCS", {"start": v(-1.79, -31.5) * mm, "end": v(-1.73, -26.5) * mm});
            skLineSegment(sketch, "E234.MirrorCS", {"start": v(4.36, 0) * mm, "end": v(4.36, -2.45) * mm});
            skLineSegment(sketch, "E235.MirrorCS", {"start": v(-23.93, -14.38) * mm, "end": v(-28.29, -16.83) * mm});
            skLineSegment(sketch, "E236.MirrorCS", {"start": v(25.7, -31.6) * mm, "end": v(25.65, -26.6) * mm});
            skLineSegment(sketch, "E237.MirrorCS", {"start": v(16.33, -16.79) * mm, "end": v(16.39, -21.79) * mm});
            skLineSegment(sketch, "E238.MirrorCS", {"start": v(-40.25, -16.88) * mm, "end": v(-40.3, -21.88) * mm});
            skLineSegment(sketch, "E239.MirrorCS", {"start": v(-34.3, -26.5) * mm, "end": v(-34.36, -31.5) * mm});
            skLineSegment(sketch, "E240.MirrorCS", {"start": v(12.09, -24.33) * mm, "end": v(7.73, -21.88) * mm});
            skLineSegment(sketch, "E241.MirrorCS", {"start": v(34.29, -12.2) * mm, "end": v(29.99, -14.76) * mm});
            skLineSegment(sketch, "E242.MirrorCS", {"start": v(7.73, -21.88) * mm, "end": v(7.67, -16.88) * mm});
            skLineSegment(sketch, "E243.MirrorCS", {"start": v(-4.5, -41.03) * mm, "end": v(0, -43.53) * mm});
            skLineSegment(sketch, "E244.MirrorCS", {"start": v(28.27, -2.54) * mm, "end": v(23.97, -5.1) * mm});
            skLineSegment(sketch, "E245.MirrorCS", {"start": v(-13.61, -7.26) * mm, "end": v(-17.92, -4.71) * mm});
            skLineSegment(sketch, "E246.MirrorCS", {"start": v(22.4, -31.45) * mm, "end": v(18.1, -34) * mm});
            skLineSegment(sketch, "E247.MirrorCS", {"start": v(-6.14, -33.96) * mm, "end": v(-1.79, -31.5) * mm});
            skLineSegment(sketch, "E248.MirrorCS", {"start": v(0, -33.48) * mm, "end": v(-4.45, -36.03) * mm});
            skLineSegment(sketch, "E249.MirrorCS", {"start": v(4.36, -2.45) * mm, "end": v(0, -5) * mm});
            skLineSegment(sketch, "E250.MirrorCS", {"start": v(1.66, -7.22) * mm, "end": v(5.96, -4.67) * mm});
            skLineSegment(sketch, "E251.MirrorCS", {"start": v(19.69, -21.93) * mm, "end": v(19.63, -16.93) * mm});
            skLineSegment(sketch, "E252.MirrorCS", {"start": v(5.96, -4.67) * mm, "end": v(10.32, -7.12) * mm});
            skLineSegment(sketch, "E253.MirrorCS", {"start": v(1.79, -31.5) * mm, "end": v(1.73, -26.5) * mm});
            skLineSegment(sketch, "E254.MirrorCS", {"start": v(4.43, -21.74) * mm, "end": v(0, -24.24) * mm});
            skLineSegment(sketch, "E255.MirrorCS", {"start": v(-25.63, -12.3) * mm, "end": v(-25.57, -7.3) * mm});
            skLineSegment(sketch, "E256.MirrorCS", {"start": v(-6.03, -23.96) * mm, "end": v(-10.39, -26.4) * mm});
            skLineSegment(sketch, "E257.MirrorCS", {"start": v(22.27, -7.16) * mm, "end": v(22.33, -12.16) * mm});
            skLineSegment(sketch, "E258.MirrorCS", {"start": v(7.74, -36.17) * mm, "end": v(12.05, -33.62) * mm});
            skLineSegment(sketch, "E259.MirrorCS", {"start": v(52.19, -2.63) * mm, "end": v(47.89, -5.18) * mm});
            skLineSegment(sketch, "E260.MirrorCS", {"start": v(4.37, -16.74) * mm, "end": v(4.43, -21.74) * mm});
            skLineSegment(sketch, "E261.MirrorCS", {"start": v(16.33, 0) * mm, "end": v(16.32, -2.5) * mm});
            skLineSegment(sketch, "E262.MirrorCS", {"start": v(-35.89, -14.43) * mm, "end": v(-40.25, -16.88) * mm});
            skLineSegment(sketch, "E263.MirrorCS", {"start": v(-12.05, -33.62) * mm, "end": v(-16.4, -36.07) * mm});
            skLineSegment(sketch, "E264.MirrorCS", {"start": v(-24.12, -43.67) * mm, "end": v(-19.76, -41.22) * mm});
            skLineSegment(sketch, "E265.MirrorCS", {"start": v(16.39, -21.79) * mm, "end": v(12.09, -24.33) * mm});
            skLineSegment(sketch, "E266.MirrorCS", {"start": v(-10.45, -31.4) * mm, "end": v(-6.14, -33.96) * mm});
            skLineSegment(sketch, "E267.MirrorCS", {"start": v(-25.57, -7.3) * mm, "end": v(-29.87, -4.76) * mm});
            skLineSegment(sketch, "E268.MirrorCS", {"start": v(31.59, -16.98) * mm, "end": v(35.89, -14.43) * mm});
            skLineSegment(sketch, "E269.MirrorCS", {"start": v(47.89, -5.18) * mm, "end": v(43.53, -2.73) * mm});
            skLineSegment(sketch, "E270.MirrorCS", {"start": v(40.23, -2.59) * mm, "end": v(35.93, -5.14) * mm});
            skLineSegment(sketch, "E271.MirrorCS", {"start": v(23.93, -14.38) * mm, "end": v(28.29, -16.83) * mm});
            skLineSegment(sketch, "E272.MirrorCS", {"start": v(22.35, -26.45) * mm, "end": v(22.4, -31.45) * mm});
            skLineSegment(sketch, "E273.MirrorCS", {"start": v(10.39, -26.4) * mm, "end": v(10.45, -31.4) * mm});
            skLineSegment(sketch, "E274.MirrorCS", {"start": v(13.74, -31.55) * mm, "end": v(13.69, -26.55) * mm});
            skLineSegment(sketch, "E275.MirrorCS", {"start": v(12.16, -43.62) * mm, "end": v(7.8, -41.17) * mm});
            skLineSegment(sketch, "E276.MirrorCS", {"start": v(-19.69, -21.93) * mm, "end": v(-19.63, -16.93) * mm});
            skLineSegment(sketch, "E277.MirrorCS", {"start": v(10.45, -31.4) * mm, "end": v(6.14, -33.96) * mm});
            skLineSegment(sketch, "E278.MirrorCS", {"start": v(-29.95, -24.05) * mm, "end": v(-34.3, -26.5) * mm});
            skLineSegment(sketch, "E279.MirrorCS", {"start": v(-16.4, -36.07) * mm, "end": v(-16.46, -41.07) * mm});
            skLineSegment(sketch, "E280.MirrorCS", {"start": v(37.53, -7.35) * mm, "end": v(41.83, -4.8) * mm});
            skLineSegment(sketch, "E281.MirrorCS", {"start": v(-29.87, -4.76) * mm, "end": v(-34.23, -7.2) * mm});
            skLineSegment(sketch, "E282.MirrorCS", {"start": v(-18.03, -14.71) * mm, "end": v(-13.67, -12.26) * mm});
            skLineSegment(sketch, "E283.MirrorCS", {"start": v(6.14, -33.96) * mm, "end": v(1.79, -31.5) * mm});
            skLineSegment(sketch, "E284.MirrorCS", {"start": v(-19.7, -36.22) * mm, "end": v(-24, -33.67) * mm});
            skLineSegment(sketch, "E285.MirrorCS", {"start": v(28.29, -16.83) * mm, "end": v(28.35, -21.83) * mm});
            skLineSegment(sketch, "E286.MirrorCS", {"start": v(-22.27, -7.16) * mm, "end": v(-22.33, -12.16) * mm});
            skLineSegment(sketch, "E287.MirrorCS", {"start": v(34.3, -26.5) * mm, "end": v(34.36, -31.5) * mm});
            skLineSegment(sketch, "E288.MirrorCS", {"start": v(41.95, -14.8) * mm, "end": v(37.59, -12.35) * mm});
            skLineSegment(sketch, "E289.MirrorCS", {"start": v(-19.63, -16.93) * mm, "end": v(-23.93, -14.38) * mm});
            skLineSegment(sketch, "E290.MirrorCS", {"start": v(18.03, -14.71) * mm, "end": v(13.67, -12.26) * mm});
            skLineSegment(sketch, "E291.MirrorCS", {"start": v(17.99, -24) * mm, "end": v(22.35, -26.45) * mm});
            skLineSegment(sketch, "E292.MirrorCS", {"start": v(40.22, 0) * mm, "end": v(40.23, -2.59) * mm});
            skLineSegment(sketch, "E293.MirrorCS", {"start": v(-43.53, -2.73) * mm, "end": v(-43.51, 0) * mm});
            skLineSegment(sketch, "E294.MirrorCS", {"start": v(-31.57, -2.69) * mm, "end": v(-31.55, 0) * mm});
            skLineSegment(sketch, "E295.MirrorCS", {"start": v(-19.61, -2.64) * mm, "end": v(-19.63, 0) * mm});
            skLineSegment(sketch, "E296.MirrorCS", {"start": v(28.28, 0) * mm, "end": v(28.27, -2.54) * mm});
            skLineSegment(sketch, "E297.MirrorCS", {"start": v(-40.22, 0) * mm, "end": v(-40.23, -2.59) * mm});
            skLineSegment(sketch, "E298.MirrorCS", {"start": v(43.53, -2.73) * mm, "end": v(43.51, 0) * mm});
            skLineSegment(sketch, "E299.MirrorCS", {"start": v(31.57, -2.69) * mm, "end": v(31.55, 0) * mm});
            skLineSegment(sketch, "E300.MirrorCS", {"start": v(19.61, -2.64) * mm, "end": v(19.63, 0) * mm});
            skLineSegment(sketch, "E301.MirrorCS", {"start": v(52.23, 0) * mm, "end": v(52.19, -2.63) * mm});
            skLineSegment(sketch, "E302.MirrorCS", {"start": v(-52.23, 0) * mm, "end": v(-52.19, -2.63) * mm});
            skLineSegment(sketch, "E303.MirrorCS", {"start": v(-28.28, 0) * mm, "end": v(-28.27, -2.54) * mm});
            skPoint(sketch, "E304.MirrorP", {"position": v(2.18, -3.73) * mm});
            skPoint(sketch, "E305.MirrorP", {"position": v(-2.18, -3.73) * mm});
            skSolve(sketch);
        }
        {
            var Q0;
            {var subQ1=sQuery(id+"F0.wireOp",EDGE,"E9.top");Q0=makeQuery(id+"F0.imprint","IMPRINT",FACE,{"disambiguationData":[TD([[makeQuery(id+"F0.imprint","IMPRINT",EDGE,{"derivedFrom":subQ1}),1.0]])]});}
            var Q1;
            {var subQ0=sQuery(id+"F0.wireOp",EDGE,"E5");var subQ1=sQuery(id+"F0.wireOp",EDGE,"E0.top");var subQ2=makeQuery(id+"F0.imprint","INTERSECT",VERTEX,{"derivedFrom":[subQ1,subQ0]});Q1=makeQuery(id+"F0.imprint","IMPRINT",FACE,{"disambiguationData":[TD([[makeQuery(id+"F0.imprint","IMPRINT",EDGE,{"disambiguationData":[TD([[subQ2,-1.0]])],"derivedFrom":subQ1}),-1.0]])]});}
            var Q2;
            {var subQ0=sQuery(id+"F0.wireOp",EDGE,"E5");var subQ1=sQuery(id+"F0.wireOp",EDGE,"E0.top");var subQ2=makeQuery(id+"F0.imprint","INTERSECT",VERTEX,{"derivedFrom":[subQ1,subQ0]});Q2=makeQuery(id+"F0.imprint","IMPRINT",FACE,{"disambiguationData":[TD([[makeQuery(id+"F0.imprint","IMPRINT",EDGE,{"disambiguationData":[TD([[subQ2,-1.0]])],"derivedFrom":subQ1}),1.0]])]});}
            var Q3;
            {var subQ0=sQuery(id+"F0.wireOp",EDGE,"E9.right");var subQ6=sQuery(id+"F0.wireOp",EDGE,"E0.top");var subQ9=makeQuery(id+"F0.imprint","INTERSECT",VERTEX,{"derivedFrom":[subQ6,subQ0]});Q3=makeQuery(id+"F0.imprint","IMPRINT",FACE,{"disambiguationData":[TD([[makeQuery(id+"F0.imprint","IMPRINT",EDGE,{"disambiguationData":[TD([[subQ9,-1.0]])],"derivedFrom":subQ6}),1.0]])]});}
            var Q4;
            {var subQ1=sQuery(id+"F0.wireOp",EDGE,"E9.right");var subQ3=sQuery(id+"F0.wireOp",EDGE,"E0.top");var subQ4=makeQuery(id+"F0.imprint","INTERSECT",VERTEX,{"derivedFrom":[subQ3,subQ1]});Q4=makeQuery(id+"F0.imprint","IMPRINT",FACE,{"disambiguationData":[TD([[makeQuery(id+"F0.imprint","IMPRINT",EDGE,{"disambiguationData":[TD([[subQ4,-1.0]])],"derivedFrom":subQ3}),-1.0]])]});}
            var Q5;
            {var subQ6=sQuery(id+"F0.wireOp",EDGE,"E0.top");var subQ9=sQuery(id+"F0.wireOp",EDGE,"E8.right");var subQ10=makeQuery(id+"F0.imprint","INTERSECT",VERTEX,{"derivedFrom":[subQ6,subQ9]});Q5=makeQuery(id+"F0.imprint","IMPRINT",FACE,{"disambiguationData":[TD([[makeQuery(id+"F0.imprint","IMPRINT",EDGE,{"disambiguationData":[TD([[subQ10,-1.0]])],"derivedFrom":subQ6}),-1.0]])]});}
            var Q6;
            {var subQ1=sQuery(id+"F0.wireOp",EDGE,"E8.top");Q6=makeQuery(id+"F0.imprint","IMPRINT",FACE,{"disambiguationData":[TD([[makeQuery(id+"F0.imprint","IMPRINT",EDGE,{"derivedFrom":subQ1}),-1.0]])]});}
            var Q7;
            {var subQ0=sQuery(id+"F0.wireOp",EDGE,"E8.right");var subQ6=sQuery(id+"F0.wireOp",EDGE,"E0.top");var subQ9=makeQuery(id+"F0.imprint","INTERSECT",VERTEX,{"derivedFrom":[subQ6,subQ0]});Q7=makeQuery(id+"F0.imprint","IMPRINT",FACE,{"disambiguationData":[TD([[makeQuery(id+"F0.imprint","IMPRINT",EDGE,{"disambiguationData":[TD([[subQ9,-1.0]])],"derivedFrom":subQ6}),1.0]])]});}
            var Q8;
            {var subQ3=sQuery(id+"F0.wireOp",EDGE,"E0.right");var subQ5=sQuery(id+"F0.wireOp",EDGE,"E7.top");var subQ6=makeQuery(id+"F0.imprint","INTERSECT",VERTEX,{"derivedFrom":[subQ3,subQ5]});Q8=makeQuery(id+"F0.imprint","IMPRINT",FACE,{"disambiguationData":[TD([[makeQuery(id+"F0.imprint","IMPRINT",EDGE,{"disambiguationData":[TD([[subQ6,-1.0]])],"derivedFrom":subQ3}),1.0]])]});}
            var Q9;
            {var subQ8=sQuery(id+"F0.wireOp",EDGE,"E7.bottom");Q9=makeQuery(id+"F0.imprint","IMPRINT",FACE,{"disambiguationData":[TD([[makeQuery(id+"F0.imprint","IMPRINT",EDGE,{"derivedFrom":subQ8}),1.0]])]});}
            var Q10;
            {var subQ6=sQuery(id+"F0.wireOp",EDGE,"E0.bottom");var subQ9=sQuery(id+"F0.wireOp",EDGE,"E7.right");var subQ10=makeQuery(id+"F0.imprint","INTERSECT",VERTEX,{"derivedFrom":[subQ6,subQ9]});Q10=makeQuery(id+"F0.imprint","IMPRINT",FACE,{"disambiguationData":[TD([[makeQuery(id+"F0.imprint","IMPRINT",EDGE,{"disambiguationData":[TD([[subQ10,-1.0]])],"derivedFrom":subQ6}),1.0]])]});}
            var Q11;
            {var subQ0=sQuery(id+"F0.wireOp",EDGE,"E7.right");var subQ6=sQuery(id+"F0.wireOp",EDGE,"E0.bottom");var subQ9=makeQuery(id+"F0.imprint","INTERSECT",VERTEX,{"derivedFrom":[subQ6,subQ0]});Q11=makeQuery(id+"F0.imprint","IMPRINT",FACE,{"disambiguationData":[TD([[makeQuery(id+"F0.imprint","IMPRINT",EDGE,{"disambiguationData":[TD([[subQ9,-1.0]])],"derivedFrom":subQ6}),-1.0]])]});}
            var Q12;
            {var subQ5=sQuery(id+"F0.wireOp",EDGE,"E1");var subQ6=sQuery(id+"F0.wireOp",EDGE,"E0.bottom");var subQ7=makeQuery(id+"F0.imprint","INTERSECT",VERTEX,{"derivedFrom":[subQ6,subQ5]});Q12=makeQuery(id+"F0.imprint","IMPRINT",FACE,{"disambiguationData":[TD([[makeQuery(id+"F0.imprint","IMPRINT",EDGE,{"disambiguationData":[TD([[subQ7,-1.0]])],"derivedFrom":subQ6}),-1.0]])]});}
            var Q13;
            {var subQ5=sQuery(id+"F0.wireOp",EDGE,"E2");var subQ6=sQuery(id+"F0.wireOp",EDGE,"E0.bottom");var subQ7=makeQuery(id+"F0.imprint","INTERSECT",VERTEX,{"derivedFrom":[subQ6,subQ5]});Q13=makeQuery(id+"F0.imprint","IMPRINT",FACE,{"disambiguationData":[TD([[makeQuery(id+"F0.imprint","IMPRINT",EDGE,{"disambiguationData":[TD([[subQ7,-1.0]])],"derivedFrom":subQ6}),1.0]])]});}
            var Q14;
            {var subQ3=sQuery(id+"F0.wireOp",EDGE,"E0.left");var subQ5=sQuery(id+"F0.wireOp",EDGE,"E6.top");var subQ7=makeQuery(id+"F0.imprint","INTERSECT",VERTEX,{"derivedFrom":[subQ3,subQ5]});Q14=makeQuery(id+"F0.imprint","IMPRINT",FACE,{"disambiguationData":[TD([[makeQuery(id+"F0.imprint","IMPRINT",EDGE,{"disambiguationData":[TD([[subQ7,-1.0]])],"derivedFrom":subQ3}),-1.0]])]});}
            var Q15;
            {var subQ1=sQuery(id+"F0.wireOp",EDGE,"E0.bottom");var subQ7=sQuery(id+"F0.wireOp",EDGE,"E6.right");var subQ9=makeQuery(id+"F0.imprint","INTERSECT",VERTEX,{"derivedFrom":[subQ1,subQ7]});Q15=makeQuery(id+"F0.imprint","IMPRINT",FACE,{"disambiguationData":[TD([[makeQuery(id+"F0.imprint","IMPRINT",EDGE,{"disambiguationData":[TD([[subQ9,-1.0]])],"derivedFrom":subQ1}),-1.0]])]});}
            var Q16;
            {var subQ3=sQuery(id+"F0.wireOp",EDGE,"E0.bottom");var subQ6=sQuery(id+"F0.wireOp",EDGE,"E6.right");var subQ8=makeQuery(id+"F0.imprint","INTERSECT",VERTEX,{"derivedFrom":[subQ3,subQ6]});Q16=makeQuery(id+"F0.imprint","IMPRINT",FACE,{"disambiguationData":[TD([[makeQuery(id+"F0.imprint","IMPRINT",EDGE,{"disambiguationData":[TD([[subQ8,-1.0]])],"derivedFrom":subQ3}),1.0]])]});}
            var Q17;
            {var subQ5=sQuery(id+"F0.wireOp",EDGE,"E2");var subQ6=sQuery(id+"F0.wireOp",EDGE,"E0.bottom");var subQ7=makeQuery(id+"F0.imprint","INTERSECT",VERTEX,{"derivedFrom":[subQ6,subQ5]});Q17=makeQuery(id+"F0.imprint","IMPRINT",FACE,{"disambiguationData":[TD([[makeQuery(id+"F0.imprint","IMPRINT",EDGE,{"disambiguationData":[TD([[subQ7,-1.0]])],"derivedFrom":subQ6}),-1.0]])]});}
            var Q18;
            {var subQ0=sQuery(id+"F0.wireOp",EDGE,"E1");var subQ1=sQuery(id+"F0.wireOp",EDGE,"E0.top");var subQ2=makeQuery(id+"F0.imprint","INTERSECT",VERTEX,{"derivedFrom":[subQ1,subQ0]});Q18=makeQuery(id+"F0.imprint","IMPRINT",FACE,{"disambiguationData":[TD([[makeQuery(id+"F0.imprint","IMPRINT",EDGE,{"disambiguationData":[TD([[subQ2,-1.0]])],"derivedFrom":subQ1}),1.0]])]});}
            var Q19;
            {var subQ0=sQuery(id+"F0.wireOp",EDGE,"E1");var subQ1=makeQuery(id+"F0.imprint","INTERSECT",VERTEX,{"derivedFrom":[sQuery(id+"F0.wireOp",EDGE,"E0.bottom"),subQ0]});Q19=makeQuery(id+"F0.imprint","IMPRINT",FACE,{"disambiguationData":[TD([[makeQuery(id+"F0.imprint","IMPRINT",EDGE,{"disambiguationData":[TD([[subQ1,1.0]])],"derivedFrom":subQ0}),1.0]])]});}
            extrude(context, id + "F2", {"entities" : qUnion([Q0, Q1, Q2, Q3, Q4, Q5, Q6, Q7, Q8, Q9, Q10, Q11, Q12, Q13, Q14, Q15, Q16, Q17, Q18, Q19]), "depth" : 2 * mm, "offsetDistance" : 25 * mm});
        }
        {
            var Q0;
            {var subQ5=sQuery(id+"F0.wireOp",EDGE,"E6.bottom");Q0=makeQuery(id+"F0.imprint","IMPRINT",FACE,{"disambiguationData":[TD([[makeQuery(id+"F0.imprint","IMPRINT",EDGE,{"derivedFrom":subQ5}),-1.0]])]});}
            var Q1;
            {var subQ3=sQuery(id+"F0.wireOp",EDGE,"E0.bottom");var subQ6=sQuery(id+"F0.wireOp",EDGE,"E6.right");var subQ8=makeQuery(id+"F0.imprint","INTERSECT",VERTEX,{"derivedFrom":[subQ3,subQ6]});Q1=makeQuery(id+"F0.imprint","IMPRINT",FACE,{"disambiguationData":[TD([[makeQuery(id+"F0.imprint","IMPRINT",EDGE,{"disambiguationData":[TD([[subQ8,-1.0]])],"derivedFrom":subQ3}),1.0]])]});}
            var Q2;
            {var subQ5=sQuery(id+"F0.wireOp",EDGE,"E2");var subQ6=sQuery(id+"F0.wireOp",EDGE,"E0.bottom");var subQ7=makeQuery(id+"F0.imprint","INTERSECT",VERTEX,{"derivedFrom":[subQ6,subQ5]});Q2=makeQuery(id+"F0.imprint","IMPRINT",FACE,{"disambiguationData":[TD([[makeQuery(id+"F0.imprint","IMPRINT",EDGE,{"disambiguationData":[TD([[subQ7,-1.0]])],"derivedFrom":subQ6}),1.0]])]});}
            var Q3;
            {var subQ5=sQuery(id+"F0.wireOp",EDGE,"E2");var subQ6=sQuery(id+"F0.wireOp",EDGE,"E0.bottom");var subQ7=makeQuery(id+"F0.imprint","INTERSECT",VERTEX,{"derivedFrom":[subQ6,subQ5]});Q3=makeQuery(id+"F0.imprint","IMPRINT",FACE,{"disambiguationData":[TD([[makeQuery(id+"F0.imprint","IMPRINT",EDGE,{"disambiguationData":[TD([[subQ7,-1.0]])],"derivedFrom":subQ6}),-1.0]])]});}
            var Q4;
            {var subQ1=sQuery(id+"F0.wireOp",EDGE,"E0.bottom");var subQ7=sQuery(id+"F0.wireOp",EDGE,"E6.right");var subQ9=makeQuery(id+"F0.imprint","INTERSECT",VERTEX,{"derivedFrom":[subQ1,subQ7]});Q4=makeQuery(id+"F0.imprint","IMPRINT",FACE,{"disambiguationData":[TD([[makeQuery(id+"F0.imprint","IMPRINT",EDGE,{"disambiguationData":[TD([[subQ9,-1.0]])],"derivedFrom":subQ1}),-1.0]])]});}
            var Q5;
            Q5=makeQuery(id+"F1.imprint","IMPRINT",FACE,{"disambiguationData":[TD([[makeQuery(id+"F1.imprint","IMPRINT",EDGE,{"derivedFrom":sQuery(id+"F1.wireOp",EDGE,"E13.0")}),1.0]])]});
            var Q6;
            {var subQ0=sQuery(id+"F0.wireOp",EDGE,"E7.right");var subQ6=sQuery(id+"F0.wireOp",EDGE,"E0.bottom");var subQ9=makeQuery(id+"F0.imprint","INTERSECT",VERTEX,{"derivedFrom":[subQ6,subQ0]});Q6=makeQuery(id+"F0.imprint","IMPRINT",FACE,{"disambiguationData":[TD([[makeQuery(id+"F0.imprint","IMPRINT",EDGE,{"disambiguationData":[TD([[subQ9,-1.0]])],"derivedFrom":subQ6}),-1.0]])]});}
            var Q7;
            {var subQ6=sQuery(id+"F0.wireOp",EDGE,"E0.bottom");var subQ9=sQuery(id+"F0.wireOp",EDGE,"E7.right");var subQ10=makeQuery(id+"F0.imprint","INTERSECT",VERTEX,{"derivedFrom":[subQ6,subQ9]});Q7=makeQuery(id+"F0.imprint","IMPRINT",FACE,{"disambiguationData":[TD([[makeQuery(id+"F0.imprint","IMPRINT",EDGE,{"disambiguationData":[TD([[subQ10,-1.0]])],"derivedFrom":subQ6}),1.0]])]});}
            var Q8;
            {var subQ8=sQuery(id+"F0.wireOp",EDGE,"E7.bottom");Q8=makeQuery(id+"F0.imprint","IMPRINT",FACE,{"disambiguationData":[TD([[makeQuery(id+"F0.imprint","IMPRINT",EDGE,{"derivedFrom":subQ8}),1.0]])]});}
            var Q9;
            {var subQ5=sQuery(id+"F0.wireOp",EDGE,"E1");var subQ6=sQuery(id+"F0.wireOp",EDGE,"E0.bottom");var subQ7=makeQuery(id+"F0.imprint","INTERSECT",VERTEX,{"derivedFrom":[subQ6,subQ5]});Q9=makeQuery(id+"F0.imprint","IMPRINT",FACE,{"disambiguationData":[TD([[makeQuery(id+"F0.imprint","IMPRINT",EDGE,{"disambiguationData":[TD([[subQ7,-1.0]])],"derivedFrom":subQ6}),-1.0]])]});}
            var Q10;
            {var subQ3=sQuery(id+"F0.wireOp",EDGE,"E0.right");var subQ5=sQuery(id+"F0.wireOp",EDGE,"E7.top");var subQ6=makeQuery(id+"F0.imprint","INTERSECT",VERTEX,{"derivedFrom":[subQ3,subQ5]});Q10=makeQuery(id+"F0.imprint","IMPRINT",FACE,{"disambiguationData":[TD([[makeQuery(id+"F0.imprint","IMPRINT",EDGE,{"disambiguationData":[TD([[subQ6,-1.0]])],"derivedFrom":subQ3}),1.0]])]});}
            var Q11;
            {var subQ0=sQuery(id+"F0.wireOp",EDGE,"E8.right");var subQ6=sQuery(id+"F0.wireOp",EDGE,"E0.top");var subQ9=makeQuery(id+"F0.imprint","INTERSECT",VERTEX,{"derivedFrom":[subQ6,subQ0]});Q11=makeQuery(id+"F0.imprint","IMPRINT",FACE,{"disambiguationData":[TD([[makeQuery(id+"F0.imprint","IMPRINT",EDGE,{"disambiguationData":[TD([[subQ9,-1.0]])],"derivedFrom":subQ6}),1.0]])]});}
            var Q12;
            {var subQ6=sQuery(id+"F0.wireOp",EDGE,"E0.top");var subQ9=sQuery(id+"F0.wireOp",EDGE,"E8.right");var subQ10=makeQuery(id+"F0.imprint","INTERSECT",VERTEX,{"derivedFrom":[subQ6,subQ9]});Q12=makeQuery(id+"F0.imprint","IMPRINT",FACE,{"disambiguationData":[TD([[makeQuery(id+"F0.imprint","IMPRINT",EDGE,{"disambiguationData":[TD([[subQ10,-1.0]])],"derivedFrom":subQ6}),-1.0]])]});}
            var Q13;
            {var subQ1=sQuery(id+"F0.wireOp",EDGE,"E8.top");Q13=makeQuery(id+"F0.imprint","IMPRINT",FACE,{"disambiguationData":[TD([[makeQuery(id+"F0.imprint","IMPRINT",EDGE,{"derivedFrom":subQ1}),-1.0]])]});}
            var Q14;
            {var subQ1=sQuery(id+"F0.wireOp",EDGE,"E9.right");var subQ3=sQuery(id+"F0.wireOp",EDGE,"E0.top");var subQ4=makeQuery(id+"F0.imprint","INTERSECT",VERTEX,{"derivedFrom":[subQ3,subQ1]});Q14=makeQuery(id+"F0.imprint","IMPRINT",FACE,{"disambiguationData":[TD([[makeQuery(id+"F0.imprint","IMPRINT",EDGE,{"disambiguationData":[TD([[subQ4,-1.0]])],"derivedFrom":subQ3}),-1.0]])]});}
            var Q15;
            {var subQ0=sQuery(id+"F0.wireOp",EDGE,"E9.right");var subQ6=sQuery(id+"F0.wireOp",EDGE,"E0.top");var subQ9=makeQuery(id+"F0.imprint","INTERSECT",VERTEX,{"derivedFrom":[subQ6,subQ0]});Q15=makeQuery(id+"F0.imprint","IMPRINT",FACE,{"disambiguationData":[TD([[makeQuery(id+"F0.imprint","IMPRINT",EDGE,{"disambiguationData":[TD([[subQ9,-1.0]])],"derivedFrom":subQ6}),1.0]])]});}
            var Q16;
            {var subQ3=sQuery(id+"F0.wireOp",EDGE,"E0.left");var subQ5=sQuery(id+"F0.wireOp",EDGE,"E6.top");var subQ7=makeQuery(id+"F0.imprint","INTERSECT",VERTEX,{"derivedFrom":[subQ3,subQ5]});Q16=makeQuery(id+"F0.imprint","IMPRINT",FACE,{"disambiguationData":[TD([[makeQuery(id+"F0.imprint","IMPRINT",EDGE,{"disambiguationData":[TD([[subQ7,-1.0]])],"derivedFrom":subQ3}),-1.0]])]});}
            var Q17;
            {var subQ0=sQuery(id+"F0.wireOp",EDGE,"E5");var subQ1=sQuery(id+"F0.wireOp",EDGE,"E0.top");var subQ2=makeQuery(id+"F0.imprint","INTERSECT",VERTEX,{"derivedFrom":[subQ1,subQ0]});Q17=makeQuery(id+"F0.imprint","IMPRINT",FACE,{"disambiguationData":[TD([[makeQuery(id+"F0.imprint","IMPRINT",EDGE,{"disambiguationData":[TD([[subQ2,-1.0]])],"derivedFrom":subQ1}),-1.0]])]});}
            var Q18;
            {var subQ1=sQuery(id+"F0.wireOp",EDGE,"E9.top");Q18=makeQuery(id+"F0.imprint","IMPRINT",FACE,{"disambiguationData":[TD([[makeQuery(id+"F0.imprint","IMPRINT",EDGE,{"derivedFrom":subQ1}),1.0]])]});}
            var Q19;
            {var subQ0=sQuery(id+"F0.wireOp",EDGE,"E5");var subQ1=sQuery(id+"F0.wireOp",EDGE,"E0.top");var subQ2=makeQuery(id+"F0.imprint","INTERSECT",VERTEX,{"derivedFrom":[subQ1,subQ0]});Q19=makeQuery(id+"F0.imprint","IMPRINT",FACE,{"disambiguationData":[TD([[makeQuery(id+"F0.imprint","IMPRINT",EDGE,{"disambiguationData":[TD([[subQ2,-1.0]])],"derivedFrom":subQ1}),1.0]])]});}
            var Q20;
            {var subQ0=sQuery(id+"F0.wireOp",EDGE,"E1");var subQ1=sQuery(id+"F0.wireOp",EDGE,"E0.top");var subQ2=makeQuery(id+"F0.imprint","INTERSECT",VERTEX,{"derivedFrom":[subQ1,subQ0]});Q20=makeQuery(id+"F0.imprint","IMPRINT",FACE,{"disambiguationData":[TD([[makeQuery(id+"F0.imprint","IMPRINT",EDGE,{"disambiguationData":[TD([[subQ2,-1.0]])],"derivedFrom":subQ1}),1.0]])]});}
            extrude(context, id + "F3", {"entities" : qUnion([Q0, Q1, Q2, Q3, Q4, Q5, Q6, Q7, Q8, Q9, Q10, Q11, Q12, Q13, Q14, Q15, Q16, Q17, Q18, Q19, Q20]), "operationType" : NewBodyOperationType.ADD, "oppositeDirection" : true, "depth" : 2 * mm, "offsetDistance" : 25 * mm});
        }
        {
            var Q0;
            Q0=makeQuery(id+"F2.opExtrude","CAP_FACE",FACE,{"disambiguationData":[OSD([sQuery(id+"F0.wireOp",EDGE,"E2"),sQuery(id+"F0.wireOp",EDGE,"E3"),sQuery(id+"F0.wireOp",EDGE,"E4"),sQuery(id+"F0.wireOp",EDGE,"E5"),sQuery(id+"F0.wireOp",EDGE,"E7.bottom"),sQuery(id+"F0.wireOp",EDGE,"E7.top"),sQuery(id+"F0.wireOp",EDGE,"E7.left"),sQuery(id+"F0.wireOp",EDGE,"E7.right"),sQuery(id+"F0.wireOp",EDGE,"E8.bottom"),sQuery(id+"F0.wireOp",EDGE,"E8.top"),sQuery(id+"F0.wireOp",EDGE,"E8.left"),sQuery(id+"F0.wireOp",EDGE,"E8.right"),sQuery(id+"F0.wireOp",EDGE,"E9.bottom"),sQuery(id+"F0.wireOp",EDGE,"E9.top"),sQuery(id+"F0.wireOp",EDGE,"E9.left"),sQuery(id+"F0.wireOp",EDGE,"E9.right"),sQuery(id+"F0.wireOp",EDGE,"E12.bottom"),sQuery(id+"F0.wireOp",EDGE,"E12.top"),sQuery(id+"F0.wireOp",EDGE,"E12.left"),sQuery(id+"F0.wireOp",EDGE,"E12.right")])],"isStart":false});
            extrude(context, id + "F4", {"entities" : qUnion([Q0]), "operationType" : NewBodyOperationType.REMOVE, "oppositeDirection" : true, "depth" : 2 * mm, "offsetDistance" : 25 * mm});
        }
        {
            var Q0;
            Q0=makeQuery(id+"F3.opExtrude","SWEPT_EDGE",EDGE,{"disambiguationData":[OSD([sQuery(id+"F0.wireOp",EDGE,"E6.right"),sQuery(id+"F0.wireOp",EDGE,"E12.bottom")])]});
            var Q1;
            Q1=makeQuery(id+"F3.opExtrude","SWEPT_EDGE",EDGE,{"disambiguationData":[OSD([sQuery(id+"F0.wireOp",EDGE,"E6.bottom"),sQuery(id+"F0.wireOp",EDGE,"E6.right")])]});
            var Q2;
            {var subQ0=sQuery(id+"F0.wireOp",EDGE,"E12.bottom");var subQ1=sQuery(id+"F0.wireOp",EDGE,"E7.right");Q2=makeQuery(id+"F3.boolean.opBoolean","MERGE",EDGE,{"derivedFrom":[makeQuery(id+"F2.opExtrude","SWEPT_EDGE",EDGE,{"disambiguationData":[OSD([subQ1,subQ0])]}),makeQuery(id+"F3.opExtrude","SWEPT_EDGE",EDGE,{"disambiguationData":[OSD([subQ1,subQ0])]})]});}
            var Q3;
            {var subQ0=sQuery(id+"F0.wireOp",EDGE,"E7.right");var subQ1=sQuery(id+"F0.wireOp",EDGE,"E7.bottom");Q3=makeQuery(id+"F3.boolean.opBoolean","MERGE",EDGE,{"derivedFrom":[makeQuery(id+"F2.opExtrude","SWEPT_EDGE",EDGE,{"disambiguationData":[OSD([subQ1,subQ0])]}),makeQuery(id+"F3.opExtrude","SWEPT_EDGE",EDGE,{"disambiguationData":[OSD([subQ1,subQ0])]})]});}
            var Q4;
            {var subQ0=sQuery(id+"F0.wireOp",EDGE,"E7.left");var subQ1=sQuery(id+"F0.wireOp",EDGE,"E7.top");Q4=makeQuery(id+"F3.boolean.opBoolean","MERGE",EDGE,{"derivedFrom":[makeQuery(id+"F2.opExtrude","SWEPT_EDGE",EDGE,{"disambiguationData":[OSD([subQ1,subQ0])]}),makeQuery(id+"F3.opExtrude","SWEPT_EDGE",EDGE,{"disambiguationData":[OSD([subQ1,subQ0])]})]});}
            var Q5;
            {var subQ0=sQuery(id+"F0.wireOp",EDGE,"E12.right");var subQ1=sQuery(id+"F0.wireOp",EDGE,"E7.top");Q5=makeQuery(id+"F3.boolean.opBoolean","MERGE",EDGE,{"derivedFrom":[makeQuery(id+"F2.opExtrude","SWEPT_EDGE",EDGE,{"disambiguationData":[OSD([subQ1,subQ0])]}),makeQuery(id+"F3.opExtrude","SWEPT_EDGE",EDGE,{"disambiguationData":[OSD([subQ1,subQ0])]})]});}
            var Q6;
            {var subQ0=sQuery(id+"F0.wireOp",EDGE,"E8.right");var subQ1=sQuery(id+"F0.wireOp",EDGE,"E8.top");Q6=makeQuery(id+"F3.boolean.opBoolean","MERGE",EDGE,{"derivedFrom":[makeQuery(id+"F2.opExtrude","SWEPT_EDGE",EDGE,{"disambiguationData":[OSD([subQ1,subQ0])]}),makeQuery(id+"F3.opExtrude","SWEPT_EDGE",EDGE,{"disambiguationData":[OSD([subQ1,subQ0])]})]});}
            var Q7;
            {var subQ0=sQuery(id+"F0.wireOp",EDGE,"E12.top");var subQ1=sQuery(id+"F0.wireOp",EDGE,"E8.right");Q7=makeQuery(id+"F3.boolean.opBoolean","MERGE",EDGE,{"derivedFrom":[makeQuery(id+"F2.opExtrude","SWEPT_EDGE",EDGE,{"disambiguationData":[OSD([subQ1,subQ0])]}),makeQuery(id+"F3.opExtrude","SWEPT_EDGE",EDGE,{"disambiguationData":[OSD([subQ1,subQ0])]})]});}
            var Q8;
            {var subQ0=sQuery(id+"F0.wireOp",EDGE,"E9.left");var subQ1=sQuery(id+"F0.wireOp",EDGE,"E9.bottom");Q8=makeQuery(id+"F3.boolean.opBoolean","MERGE",EDGE,{"derivedFrom":[makeQuery(id+"F2.opExtrude","SWEPT_EDGE",EDGE,{"disambiguationData":[OSD([subQ1,subQ0])]}),makeQuery(id+"F3.opExtrude","SWEPT_EDGE",EDGE,{"disambiguationData":[OSD([subQ1,subQ0])]})]});}
            var Q9;
            {var subQ0=sQuery(id+"F0.wireOp",EDGE,"E12.left");var subQ1=sQuery(id+"F0.wireOp",EDGE,"E9.bottom");Q9=makeQuery(id+"F3.boolean.opBoolean","MERGE",EDGE,{"derivedFrom":[makeQuery(id+"F2.opExtrude","SWEPT_EDGE",EDGE,{"disambiguationData":[OSD([subQ1,subQ0])]}),makeQuery(id+"F3.opExtrude","SWEPT_EDGE",EDGE,{"disambiguationData":[OSD([subQ1,subQ0])]})]});}
            var Q10;
            Q10=makeQuery(id+"F3.opExtrude","SWEPT_EDGE",EDGE,{"disambiguationData":[OSD([sQuery(id+"F0.wireOp",EDGE,"E6.top"),sQuery(id+"F0.wireOp",EDGE,"E12.left")])]});
            var Q11;
            Q11=makeQuery(id+"F3.opExtrude","SWEPT_EDGE",EDGE,{"disambiguationData":[OSD([sQuery(id+"F0.wireOp",EDGE,"E6.top"),sQuery(id+"F0.wireOp",EDGE,"E6.left")])]});
            var Q12;
            {var subQ0=sQuery(id+"F0.wireOp",EDGE,"E9.right");var subQ1=sQuery(id+"F0.wireOp",EDGE,"E9.top");Q12=makeQuery(id+"F3.boolean.opBoolean","MERGE",EDGE,{"derivedFrom":[makeQuery(id+"F2.opExtrude","SWEPT_EDGE",EDGE,{"disambiguationData":[OSD([subQ1,subQ0])]}),makeQuery(id+"F3.opExtrude","SWEPT_EDGE",EDGE,{"disambiguationData":[OSD([subQ1,subQ0])]})]});}
            var Q13;
            {var subQ0=sQuery(id+"F0.wireOp",EDGE,"E12.top");var subQ1=sQuery(id+"F0.wireOp",EDGE,"E9.right");Q13=makeQuery(id+"F3.boolean.opBoolean","MERGE",EDGE,{"derivedFrom":[makeQuery(id+"F2.opExtrude","SWEPT_EDGE",EDGE,{"disambiguationData":[OSD([subQ1,subQ0])]}),makeQuery(id+"F3.opExtrude","SWEPT_EDGE",EDGE,{"disambiguationData":[OSD([subQ1,subQ0])]})]});}
            var Q14;
            {var subQ0=sQuery(id+"F0.wireOp",EDGE,"E12.right");var subQ1=sQuery(id+"F0.wireOp",EDGE,"E8.bottom");Q14=makeQuery(id+"F3.boolean.opBoolean","MERGE",EDGE,{"derivedFrom":[makeQuery(id+"F2.opExtrude","SWEPT_EDGE",EDGE,{"disambiguationData":[OSD([subQ1,subQ0])]}),makeQuery(id+"F3.opExtrude","SWEPT_EDGE",EDGE,{"disambiguationData":[OSD([subQ1,subQ0])]})]});}
            var Q15;
            {var subQ0=sQuery(id+"F0.wireOp",EDGE,"E8.left");var subQ1=sQuery(id+"F0.wireOp",EDGE,"E8.bottom");Q15=makeQuery(id+"F3.boolean.opBoolean","MERGE",EDGE,{"derivedFrom":[makeQuery(id+"F2.opExtrude","SWEPT_EDGE",EDGE,{"disambiguationData":[OSD([subQ1,subQ0])]}),makeQuery(id+"F3.opExtrude","SWEPT_EDGE",EDGE,{"disambiguationData":[OSD([subQ1,subQ0])]})]});}
            fillet(context, id + "F5", {"entities" : qUnion([Q0, Q1, Q2, Q3, Q4, Q5, Q6, Q7, Q8, Q9, Q10, Q11, Q12, Q13, Q14, Q15]), "radius" : 2.5 * mm, "tangentPropagation" : true, "allowEdgeOverflow" : false});
        }
        {
            var Q0;
            Q0=makeQuery(id+"F3.opExtrude","SWEPT_EDGE",EDGE,{"disambiguationData":[OSD([sQuery(id+"F0.wireOp",EDGE,"E6.bottom"),sQuery(id+"F0.wireOp",EDGE,"E6.left")])]});
            var Q1;
            {var subQ0=sQuery(id+"F0.wireOp",EDGE,"E7.left");var subQ1=sQuery(id+"F0.wireOp",EDGE,"E7.bottom");Q1=makeQuery(id+"F3.boolean.opBoolean","MERGE",EDGE,{"derivedFrom":[makeQuery(id+"F2.opExtrude","SWEPT_EDGE",EDGE,{"disambiguationData":[OSD([subQ1,subQ0])]}),makeQuery(id+"F3.opExtrude","SWEPT_EDGE",EDGE,{"disambiguationData":[OSD([subQ1,subQ0])]})]});}
            var Q2;
            {var subQ0=sQuery(id+"F0.wireOp",EDGE,"E8.left");var subQ1=sQuery(id+"F0.wireOp",EDGE,"E8.top");Q2=makeQuery(id+"F3.boolean.opBoolean","MERGE",EDGE,{"derivedFrom":[makeQuery(id+"F2.opExtrude","SWEPT_EDGE",EDGE,{"disambiguationData":[OSD([subQ1,subQ0])]}),makeQuery(id+"F3.opExtrude","SWEPT_EDGE",EDGE,{"disambiguationData":[OSD([subQ1,subQ0])]})]});}
            var Q3;
            {var subQ0=sQuery(id+"F0.wireOp",EDGE,"E9.left");var subQ1=sQuery(id+"F0.wireOp",EDGE,"E9.top");Q3=makeQuery(id+"F3.boolean.opBoolean","MERGE",EDGE,{"derivedFrom":[makeQuery(id+"F2.opExtrude","SWEPT_EDGE",EDGE,{"disambiguationData":[OSD([subQ1,subQ0])]}),makeQuery(id+"F3.opExtrude","SWEPT_EDGE",EDGE,{"disambiguationData":[OSD([subQ1,subQ0])]})]});}
            fillet(context, id + "F6", {"entities" : qUnion([Q0, Q1, Q2, Q3]), "radius" : 10 * mm, "tangentPropagation" : true, "allowEdgeOverflow" : false});
        }
    });
